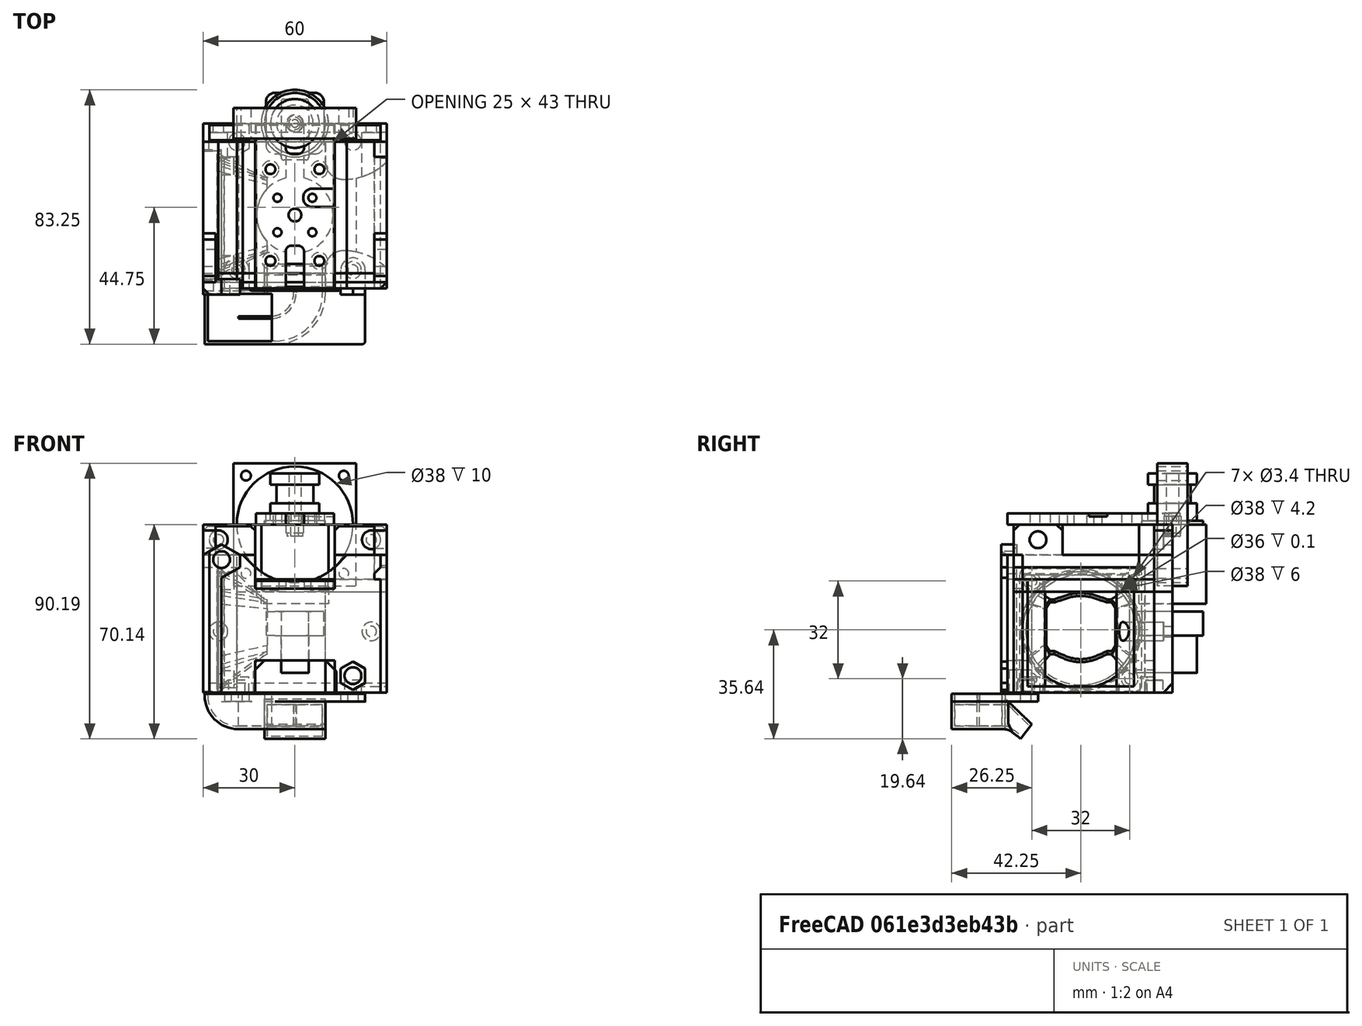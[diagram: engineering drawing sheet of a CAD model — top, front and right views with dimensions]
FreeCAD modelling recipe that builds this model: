
FCSTD DOCUMENT  (FreeCAD 1.0R39319 (Git))
Label: TAZ-EVO-Dragon-v0.4
License: All rights reserved
LicenseURL: https://en.wikipedia.org/wiki/All_rights_reserved
objects: Sketcher::SketchObject×53, PartDesign::Body×28, PartDesign::Pad×24, PartDesign::Pocket×20, App::Part×18, PartDesign::SubShapeBinder×17, PartDesign::FeatureBase×14, PartDesign::Fillet×11, PartDesign::Chamfer×9, PartDesign::Hole×5, PartDesign::Plane×4, App::DocumentObjectGroup×3, PartDesign::AdditiveLoft×2, PartDesign::Revolution×1, Mesh::Feature×1, PartDesign::Mirrored×1, PartDesign::Boolean×1, Spreadsheet::Sheet×1
note: 403 computed .brp shape members not serialized (recipe doc carries the construction recipe); baked Part::Feature solids carry a one-line shape summary decoded from their .brp

FEATURE [Sketcher::SketchObject] Sketch  label="Mount Plate Sk"
  ArcFitTolerance = 1e-06
  FullyConstrained = true
  MakeInternals = false
  Placement = pos=(0,0,0) rot=(1,0,0;1.5708rad)
  sketch-geometry (18):
    g0: LineSegment StartX=-30 StartY=55 StartZ=0 EndX=-30 EndY=-55 EndZ=0
    g1: LineSegment StartX=-30 StartY=-55 StartZ=0 EndX=30 EndY=-55 EndZ=0
    g2: LineSegment StartX=30 StartY=-55 StartZ=0 EndX=30 EndY=55 EndZ=0
    g3: LineSegment StartX=30 StartY=55 StartZ=0 EndX=-30 EndY=55 EndZ=0
    g4: Circle CenterX=-18 CenterY=50 CenterZ=0 NormalX=0 NormalY=0 NormalZ=1 AngleXU=0 Radius=1.7
    g5: Circle CenterX=18 CenterY=50 CenterZ=0 NormalX=0 NormalY=0 NormalZ=1 AngleXU=0 Radius=1.7
    g6: Circle CenterX=-18 CenterY=-50 CenterZ=0 NormalX=0 NormalY=0 NormalZ=1 AngleXU=0 Radius=1.7
    g7: Circle CenterX=18 CenterY=-50 CenterZ=0 NormalX=0 NormalY=0 NormalZ=1 AngleXU=0 Radius=1.7
    g8: Circle CenterX=-25 CenterY=35 CenterZ=0 NormalX=0 NormalY=0 NormalZ=1 AngleXU=0 Radius=1.7
    g9: Circle CenterX=-25 CenterY=5 CenterZ=0 NormalX=0 NormalY=0 NormalZ=1 AngleXU=0 Radius=1.7
    g10: Circle CenterX=-25 CenterY=-5 CenterZ=0 NormalX=0 NormalY=0 NormalZ=1 AngleXU=0 Radius=1.7
    g11: Circle CenterX=-25 CenterY=-35 CenterZ=0 NormalX=0 NormalY=0 NormalZ=1 AngleXU=0 Radius=1.7
    g12: Circle CenterX=25 CenterY=35 CenterZ=0 NormalX=0 NormalY=0 NormalZ=1 AngleXU=0 Radius=1.7
    g13: Circle CenterX=25 CenterY=5 CenterZ=0 NormalX=0 NormalY=0 NormalZ=1 AngleXU=0 Radius=1.7
    g14: Circle CenterX=25 CenterY=-5 CenterZ=0 NormalX=0 NormalY=0 NormalZ=1 AngleXU=0 Radius=1.7
    g15: Circle CenterX=25 CenterY=-35 CenterZ=0 NormalX=0 NormalY=0 NormalZ=1 AngleXU=0 Radius=1.7
    g16: LineSegment [constr] StartX=-25 StartY=35 StartZ=0 EndX=-25 EndY=-35 EndZ=0
    g17: LineSegment [constr] StartX=25 StartY=35 StartZ=0 EndX=25 EndY=-35 EndZ=0
  constraints (41):
    c: Coincident(g0,g1)
    c: Coincident(g1,g2)
    c: Coincident(g2,g3)
    c: Coincident(g3,g0)
    c: Vertical(g0)
    c: Horizontal(g3)
    c: DistanceX(g3,g3) = 60
    c: Symmetric(g8,g12,g-2)
    c: Symmetric(g11,g15,g-2)
    c: DistanceX(g8,g12) = 50
    c: Symmetric(g4,g5,g-2)
    c: DistanceX(g4,g5) = 36
    c: Symmetric(g11,g8,g-1)
    c: Coincident(g16,g8)
    c: Coincident(g16,g11)
    c: Coincident(g17,g12)
    c: Coincident(g17,g15)
    c: PointOnObject(g9,g16)
    c: DistanceY(g10,g9) = 10
    c: Symmetric(g6,g7,g-2)
    c: Symmetric(g6,g4,g-1)
    c: DistanceY(g6,g4) = 100
    c: Symmetric(g0,g1,g-2)
    c: Symmetric(g1,g2,g-1)
    c: DistanceY(g13,g12) = 30
    c: Equal(g8,g12)
    c: Equal(g9,g13)
    c: Equal(g10,g14)
    c: Equal(g11,g15)
    c: Equal(g6,g7)
    c: DistanceY(g2,g2) = 110
    c: Diameter(g13) = 3.4
    c: Equal(g5,g4)
    c: Equal(g13,g14)
    c: Equal(g14,g15)
    c: Equal(g15,g7)
    c: Equal(g5,g7)
    c: Equal(g13,g12)
    c: Symmetric(g9,g13,g-2)
    c: Symmetric(g13,g14,g-1)
    c: Symmetric(g9,g10,g-1)
FEATURE [Sketcher::SketchObject] Sketch001
  ArcFitTolerance = 1e-06
  AttachmentSupport = -> [XY_Plane001]
  FullyConstrained = true
  MakeInternals = false
  MapMode = 5
  sketch-geometry (1):
    g0: Circle CenterX=0 CenterY=0 CenterZ=0 NormalX=0 NormalY=0 NormalZ=1 AngleXU=0 Radius=11
  constraints (2):
    c: Coincident(g0,g-1)
    c: Diameter(g0) = 22
FEATURE [PartDesign::Pad] Pad
  Direction = (0,0,1)
  Length = 26
  Length2 = 10
  Profile = -> Sketch001
  ReferenceAxis = -> Sketch001 [N_Axis]
  Refine = true
  Reversed = true
  Suppressed = false
  Type = 0
FEATURE [PartDesign::Body] Body  label="HeatBreak"
  AllowCompound = false
  Group = -> [Sketch001,Pad]
  Origin = -> Origin001
  Tip = -> Pad
FEATURE [Sketcher::SketchObject] Sketch002
  ArcFitTolerance = 1e-06
  AttachmentSupport = -> [XZ_Plane002]
  FullyConstrained = true
  MakeInternals = false
  MapMode = 5
  Placement = pos=(0,0,0) rot=(1,0,0;1.5708rad)
  sketch-geometry (9):
    g0: LineSegment StartX=-9.5 StartY=0 StartZ=0 EndX=-9.5 EndY=-7.85 EndZ=0
    g1: LineSegment StartX=-9.5 StartY=-7.85 StartZ=0 EndX=-4.5 EndY=-7.85 EndZ=0
    g2: LineSegment StartX=-4.5 StartY=-7.85 StartZ=0 EndX=-4.5 EndY=-20 EndZ=0
    g3: LineSegment StartX=-4.5 StartY=-20 StartZ=0 EndX=4.5 EndY=-20 EndZ=0
    g4: LineSegment StartX=4.5 StartY=-20 StartZ=0 EndX=4.5 EndY=-7.85 EndZ=0
    g5: LineSegment StartX=4.5 StartY=-7.85 StartZ=0 EndX=9.5 EndY=-7.85 EndZ=0
    g6: LineSegment StartX=9.5 StartY=-7.85 StartZ=0 EndX=9.5 EndY=0 EndZ=0
    g7: LineSegment StartX=9.5 StartY=0 StartZ=0 EndX=-9.5 EndY=0 EndZ=0
    g8: LineSegment [constr] StartX=-4.5 StartY=-7.85 StartZ=0 EndX=4.5 EndY=-7.85 EndZ=0
  constraints (24):
    c: PointOnObject(g0,g-1)
    c: Vertical(g0)
    c: Coincident(g0,g1)
    c: Coincident(g1,g2)
    c: Vertical(g2)
    c: Coincident(g2,g3)
    c: Coincident(g3,g4)
    c: Vertical(g4)
    c: Coincident(g4,g5)
    c: Coincident(g5,g6)
    c: Vertical(g6)
    c: Coincident(g6,g7)
    c: Coincident(g7,g0)
    c: Coincident(g8,g1)
    c: Coincident(g8,g4)
    c: Horizontal(g8)
    c: Horizontal(g5)
    c: Horizontal(g1)
    c: Symmetric(g2,g3,g-2)
    c: Symmetric(g0,g6,g-2)
    c: DistanceY(g3,g6) = 20
    c: DistanceX(g3,g3) = 9
    c: DistanceX(g7,g7) = 19
    c: DistanceY(g0,g0) = 7.85
FEATURE [PartDesign::Pad] Pad001
  Direction = (0,-1,2e-16)
  Length = 20
  Length2 = 10
  Midplane = true
  Placement = pos=(0,0,0) rot=(1,0,0;1.5708rad)
  Profile = -> Sketch002
  ReferenceAxis = -> Sketch002 [N_Axis]
  Refine = true
  Suppressed = false
  Type = 0
FEATURE [Sketcher::SketchObject] Sketch003
  ArcFitTolerance = 1e-06
  AttachmentSupport = -> [Pad001]
  ExternalGeometry = -> [Pad001]
  FullyConstrained = true
  MakeInternals = false
  MapMode = 5
  Placement = pos=(0,-10,0) rot=(1,0,0;1.5708rad)
  sketch-geometry (4):
    g0: LineSegment StartX=-4.5 StartY=-20 StartZ=0 EndX=4.5 EndY=-20 EndZ=0
    g1: LineSegment StartX=4.5 StartY=-20 StartZ=0 EndX=4.5 EndY=0 EndZ=0
    g2: LineSegment StartX=4.5 StartY=0 StartZ=0 EndX=-4.5 EndY=0 EndZ=0
    g3: LineSegment StartX=-4.5 StartY=0 StartZ=0 EndX=-4.5 EndY=-20 EndZ=0
  constraints (10):
    c: Coincident(g0,g1)
    c: Coincident(g1,g2)
    c: Coincident(g2,g3)
    c: Coincident(g3,g0)
    c: Horizontal(g2)
    c: Vertical(g1)
    c: Vertical(g3)
    c: Coincident(g0,g-3)
    c: PointOnObject(g1,g-1)
    c: Coincident(g0,g-3)
FEATURE [PartDesign::Pad] Pad002
  BaseFeature = -> Pad001
  Direction = (0,-1,2e-16)
  Length = 2
  Length2 = 10
  Placement = pos=(0,0,0) rot=(1,0,0;1.5708rad)
  Profile = -> Sketch003
  ReferenceAxis = -> Sketch003 [N_Axis]
  Refine = true
  Suppressed = false
  Type = 0
FEATURE [Sketcher::SketchObject] Sketch004
  ArcFitTolerance = 1e-06
  AttachmentSupport = -> [Pad002]
  ExternalGeometry = -> [Pad002]
  FullyConstrained = true
  MakeInternals = false
  MapMode = 5
  Placement = pos=(0,10,0) rot=(-1,0,0;1.5708rad)
  sketch-geometry (4):
    g0: LineSegment StartX=-4.5 StartY=20 StartZ=0 EndX=-4.5 EndY=7.85 EndZ=0
    g1: LineSegment StartX=-4.5 StartY=7.85 StartZ=0 EndX=4.5 EndY=7.85 EndZ=0
    g2: LineSegment StartX=4.5 StartY=7.85 StartZ=0 EndX=4.5 EndY=20 EndZ=0
    g3: LineSegment StartX=4.5 StartY=20 StartZ=0 EndX=-4.5 EndY=20 EndZ=0
  constraints (10):
    c: Coincident(g0,g1)
    c: Coincident(g1,g2)
    c: Coincident(g2,g3)
    c: Coincident(g3,g0)
    c: Vertical(g0)
    c: Vertical(g2)
    c: Horizontal(g1)
    c: Horizontal(g3)
    c: Coincident(g0,g-3)
    c: Coincident(g1,g-4)
FEATURE [PartDesign::Pocket] Pocket
  BaseFeature = -> Pad002
  Direction = (0,-1,-2e-16)
  Length = 2
  Length2 = 5
  Placement = pos=(0,0,0) rot=(1,0,0;1.5708rad)
  Profile = -> Sketch004
  ReferenceAxis = -> Sketch004 [N_Axis]
  Refine = true
  Suppressed = false
  Type = 0
FEATURE [PartDesign::Fillet] Fillet
  Base = -> Pocket [Edge19,Edge23,Edge27,Edge21,Edge25,Edge15]
  BaseFeature = -> Pocket
  Placement = pos=(0,0,0) rot=(1,0,0;1.5708rad)
  Radius = 0.9
  Refine = true
  SupportTransform = false
  Suppressed = false
  UseAllEdges = false
FEATURE [PartDesign::Fillet] Fillet001
  Base = -> Fillet [Edge15,Edge19,Edge30,Edge26]
  BaseFeature = -> Fillet
  Placement = pos=(0,0,0) rot=(1,0,0;1.5708rad)
  Radius = 3
  Refine = true
  SupportTransform = false
  Suppressed = false
  UseAllEdges = false
FEATURE [PartDesign::Body] Body001  label="HeatBlock"
  AllowCompound = false
  Group = -> [Sketch002,Pad001,Sketch003,Pad002,Sketch004,Pocket,Fillet,Fillet001]
  Origin = -> Origin002
  Placement = pos=(0,0,-28.5) rot=(0,0,1;0rad)
  Tip = -> Fillet001
FEATURE [Sketcher::SketchObject] Sketch005
  ArcFitTolerance = 1e-06
  AttachmentSupport = -> [XZ_Plane003]
  FullyConstrained = true
  MakeInternals = false
  MapMode = 5
  Placement = pos=(0,0,0) rot=(1,0,0;1.5708rad)
  sketch-geometry (11):
    g0: LineSegment StartX=0 StartY=0 StartZ=0 EndX=10 EndY=0 EndZ=0
    g1: LineSegment StartX=10 StartY=0 StartZ=0 EndX=10 EndY=1.25 EndZ=0
    g2: LineSegment StartX=10 StartY=1.25 StartZ=0 EndX=8 EndY=1.25 EndZ=0
    g3: LineSegment StartX=8 StartY=1.25 StartZ=0 EndX=8 EndY=7 EndZ=0
    g4: LineSegment StartX=8 StartY=7 StartZ=0 EndX=6 EndY=7 EndZ=0
    g5: LineSegment StartX=6 StartY=7 StartZ=0 EndX=6 EndY=13.05 EndZ=0
    g6: LineSegment StartX=6 StartY=13.05 StartZ=0 EndX=8 EndY=13.05 EndZ=0
    g7: LineSegment StartX=8 StartY=13.05 StartZ=0 EndX=8 EndY=16.75 EndZ=0
    g8: LineSegment StartX=8 StartY=16.75 StartZ=0 EndX=0 EndY=16.75 EndZ=0
    g9: LineSegment StartX=0 StartY=16.75 StartZ=0 EndX=0 EndY=0 EndZ=0
    g10: LineSegment [constr] StartX=8 StartY=13.05 StartZ=0 EndX=8 EndY=7 EndZ=0
  constraints (31):
    c: Coincident(g-1,g0)
    c: PointOnObject(g0,g-1)
    c: Coincident(g0,g1)
    c: Vertical(g1)
    c: Coincident(g1,g2)
    c: Horizontal(g2)
    c: Coincident(g2,g3)
    c: Coincident(g3,g4)
    c: Horizontal(g4)
    c: Coincident(g4,g5)
    c: Vertical(g5)
    c: Coincident(g5,g6)
    c: Horizontal(g6)
    c: Coincident(g6,g7)
    c: Coincident(g7,g8)
    c: Horizontal(g8)
    c: Coincident(g8,g9)
    c: Coincident(g9,g0)
    c: Vertical(g9)
    c: DistanceX(g0,g0) = 10
    c: DistanceY(g1,g1) = 1.25
    c: Vertical(g3)
    c: DistanceY(g0,g3) = 7
    c: Vertical(g7)
    c: DistanceY(g9,g9) = 16.75
    c: DistanceY(g7,g7) = 3.7
    c: DistanceX(g8,g8) = 8
    c: Coincident(g10,g6)
    c: Coincident(g10,g3)
    c: Vertical(g10)
    c: DistanceX(g0,g4) = 6
FEATURE [PartDesign::Revolution] Revolution
  Angle = 360
  Angle2 = 60
  Axis = (0,2e-16,1)
  Base = (0,0,0)
  Placement = pos=(0,0,0) rot=(1,0,0;1.5708rad)
  Profile = -> Sketch005
  ReferenceAxis = -> Sketch005 [V_Axis]
  Refine = true
  Reversed = true
  Suppressed = false
  Type = 0
FEATURE [PartDesign::Hole] Hole
  BaseFeature = -> Revolution
  CustomThreadClearance = 0
  Depth = 25
  DepthType = 0
  Diameter = 4
  DrillForDepth = false
  DrillPoint = 1
  DrillPointAngle = 118
  HoleCutCountersinkAngle = 90
  HoleCutCustomValues = false
  HoleCutDepth = 0
  HoleCutDiameter = 6.1
  HoleCutType = 0
  ModelThread = false
  Placement = pos=(0,0,0) rot=(1,0,0;1.5708rad)
  Profile = -> Revolution [Face9]
  Refine = true
  Suppressed = false
  Tapered = false
  TaperedAngle = 90
  ThreadClass = 0
  ThreadDepth = 25
  ThreadDepthType = 0
  ThreadDirection = 0
  ThreadFit = 0
  ThreadSize = 0
  ThreadType = 0
  Threaded = false
  UseCustomThreadClearance = false
FEATURE [PartDesign::Body] Body002  label="Adapter"
  AllowCompound = false
  Group = -> [Sketch005,Revolution,Hole]
  Origin = -> Origin003
  Tip = -> Hole
FEATURE [App::Part] Part  label="Hotend"
  Group = -> [Body,Body001,Body002]
  Origin = -> Origin
  Placement = pos=(0,-30,-18.5) rot=(0,0,1;0rad)
FEATURE [Sketcher::SketchObject] Sketch006  label="FilamentPath"
  ArcFitTolerance = 1e-06
  FullyConstrained = true
  MakeInternals = false
  sketch-geometry (1):
    g0: Circle CenterX=0 CenterY=-30 CenterZ=0 NormalX=0 NormalY=0 NormalZ=1 AngleXU=0 Radius=0.875
  constraints (3):
    c: PointOnObject(g0,g-2)
    c: Diameter(g0) = 1.75
    c: DistanceY(g0,g-1) = 30
FEATURE [Sketcher::SketchObject] Sketch008
  ArcFitTolerance = 1e-06
  AttachmentSupport = -> [XZ_Plane007]
  FullyConstrained = true
  MakeInternals = false
  MapMode = 5
  Placement = pos=(0,0,0) rot=(1,0,0;1.5708rad)
  sketch-geometry (13):
    g0: Circle CenterX=0 CenterY=0 CenterZ=0 NormalX=0 NormalY=0 NormalZ=1 AngleXU=0 Radius=19
    g1: LineSegment StartX=-20.05 StartY=20.05 StartZ=0 EndX=-20.05 EndY=-20.05 EndZ=0
    g2: LineSegment StartX=-20.05 StartY=-20.05 StartZ=0 EndX=20.05 EndY=-20.05 EndZ=0
    g3: LineSegment StartX=20.05 StartY=-20.05 StartZ=0 EndX=20.05 EndY=20.05 EndZ=0
    g4: LineSegment StartX=20.05 StartY=20.05 StartZ=0 EndX=-20.05 EndY=20.05 EndZ=0
    g5: Circle CenterX=-16 CenterY=16 CenterZ=0 NormalX=0 NormalY=0 NormalZ=1 AngleXU=0 Radius=1.6
    g6: Circle CenterX=-16 CenterY=-16 CenterZ=0 NormalX=0 NormalY=0 NormalZ=1 AngleXU=0 Radius=1.6
    g7: Circle CenterX=16 CenterY=-16 CenterZ=0 NormalX=0 NormalY=0 NormalZ=1 AngleXU=0 Radius=1.6
    g8: Circle CenterX=16 CenterY=16 CenterZ=0 NormalX=0 NormalY=0 NormalZ=1 AngleXU=0 Radius=1.6
    g9: LineSegment [constr] StartX=-16 StartY=16 StartZ=0 EndX=16 EndY=16 EndZ=0
    g10: LineSegment [constr] StartX=16 StartY=16 StartZ=0 EndX=16 EndY=-16 EndZ=0
    g11: LineSegment [constr] StartX=16 StartY=-16 StartZ=0 EndX=-16 EndY=-16 EndZ=0
    g12: LineSegment [constr] StartX=-16 StartY=-16 StartZ=0 EndX=-16 EndY=16 EndZ=0
  constraints (30):
    c: Coincident(g0,g-1)
    c: Coincident(g1,g2)
    c: Coincident(g2,g3)
    c: Coincident(g3,g4)
    c: Coincident(g4,g1)
    c: Vertical(g1)
    c: Horizontal(g2)
    c: DistanceY(g3,g3) = 40.1
    c: Equal(g3,g2)
    c: Symmetric(g3,g2,g-1)
    c: Symmetric(g3,g1,g-2)
    c: Diameter(g0) = 38
    c: Coincident(g9,g5)
    c: Coincident(g9,g8)
    c: Horizontal(g9)
    c: Coincident(g10,g8)
    c: Coincident(g10,g7)
    c: Vertical(g10)
    c: Coincident(g11,g7)
    c: Coincident(g11,g6)
    c: Coincident(g12,g6)
    c: Coincident(g12,g5)
    c: DistanceY(g12,g12) = 32
    c: Equal(g12,g9)
    c: Symmetric(g7,g6,g-2)
    c: Symmetric(g6,g5,g-1)
    c: Equal(g6,g5)
    c: Equal(g5,g8)
    c: Equal(g5,g7)
    c: Diameter(g6) = 3.2
FEATURE [PartDesign::Pad] Pad003
  Direction = (0,-1,2e-16)
  Length = 10
  Length2 = 10
  Midplane = true
  Placement = pos=(0,0,0) rot=(1,0,0;1.5708rad)
  Profile = -> Sketch008
  ReferenceAxis = -> Sketch008 [N_Axis]
  Refine = true
  Suppressed = false
  Type = 0
FEATURE [PartDesign::Body] Body004
  AllowCompound = false
  Group = -> [Sketch008,Pad003]
  Origin = -> Origin007
  Placement = pos=(0,-1.8e-15,6e-16) rot=(0,0,1;0rad)
  Tip = -> Pad003
FEATURE [App::Part] Part003  label="4010 Cooling"
  Group = -> [Body004]
  Origin = -> Origin008
  Placement = pos=(-30,-30,-34.5) rot=(0,0,1;4.71239rad)
FEATURE [Mesh::Feature] Radial_Fan_50x15_v8
  Placement = pos=(-44,6,92) rot=(0,0,1;0rad)
FEATURE [App::Part] Part004  label="5015 Part"
  Group = -> [Radial_Fan_50x15_v8]
  Origin = -> Origin010
  Placement = pos=(-28.5,-71,-57) rot=(1,0,0;1.5708rad)
FEATURE [App::DocumentObjectGroup] Group001  label="Fans"
  Group = -> [Part003,Part004]
FEATURE [Sketcher::SketchObject] Sketch011
  ArcFitTolerance = 1e-06
  AttachmentSupport = -> [XY_Plane012]
  FullyConstrained = true
  MakeInternals = false
  MapMode = 5
  sketch-geometry (1):
    g0: Circle CenterX=0 CenterY=0 CenterZ=0 NormalX=0 NormalY=0 NormalZ=1 AngleXU=0 Radius=2.8
  constraints (2):
    c: Diameter(g0) = 5.6
    c: Coincident(g0,g-1)
FEATURE [PartDesign::Pad] Pad005
  Direction = (0,0,1)
  Length = 3.8
  Length2 = 10
  Profile = -> Sketch011
  ReferenceAxis = -> Sketch011 [N_Axis]
  Refine = true
  Suppressed = false
  Type = 0
FEATURE [PartDesign::Hole] Hole001
  BaseFeature = -> Pad005
  CustomThreadClearance = 0
  Depth = 17.7438
  DepthType = 0
  Diameter = 2.5
  DrillForDepth = false
  DrillPoint = 1
  DrillPointAngle = 118
  HoleCutCountersinkAngle = 90
  HoleCutCustomValues = false
  HoleCutDepth = 0
  HoleCutDiameter = 6.1
  HoleCutType = 0
  ModelThread = false
  Profile = -> Pad005 [Edge3]
  Refine = true
  Suppressed = false
  Tapered = false
  TaperedAngle = 90
  ThreadClass = 0
  ThreadDepth = 17.7438
  ThreadDepthType = 0
  ThreadDirection = 0
  ThreadFit = 1
  ThreadSize = 9
  ThreadType = 1
  Threaded = true
  UseCustomThreadClearance = false
FEATURE [Sketcher::SketchObject] Sketch012
  ArcFitTolerance = 1e-06
  AttachmentSupport = -> [Hole001]
  ExternalGeometry = -> [Hole001]
  FullyConstrained = false
  MakeInternals = false
  MapMode = 5
  Placement = pos=(0,0,3.8) rot=(0,0,1;0rad)
  sketch-geometry (2):
    g0: Circle CenterX=0 CenterY=0 CenterZ=0 NormalX=0 NormalY=0 NormalZ=1 AngleXU=0 Radius=2.575
    g1: Circle CenterX=0 CenterY=0 CenterZ=0 NormalX=0 NormalY=0 NormalZ=1 AngleXU=0 Radius=2.8
  constraints (3):
    c: Coincident(g0,g-1)
    c: Diameter(g0) = 5.15
    c: Coincident(g1,g0)
FEATURE [PartDesign::Pocket] Pocket001
  BaseFeature = -> Hole001
  Direction = (0,0,-1)
  Length = 1
  Length2 = 5
  Profile = -> Sketch012
  ReferenceAxis = -> Sketch012 [N_Axis]
  Refine = true
  Suppressed = false
  Type = 0
FEATURE [PartDesign::Body] Body006  label="M3InsertBody01"
  AllowCompound = false
  Group = -> [Sketch011,Pad005,Hole001,Sketch012,Pocket001]
  Origin = -> Origin012
  Tip = -> Pocket001
FEATURE [App::Part] Part005  label="Insert001"
  Group = -> [Body006]
  Origin = -> Origin011
  Placement = pos=(-18,-52,-12) rot=(1,0,0;4.71239rad)
FEATURE [PartDesign::FeatureBase] Clone001
  BaseFeature = -> Body006
  Suppressed = false
FEATURE [PartDesign::Body] Body007
  AllowCompound = false
  Group = -> [Clone001]
  Origin = -> Origin014
  Tip = -> Clone001
FEATURE [App::Part] Part006  label="Insert002"
  Group = -> [Body007]
  Origin = -> Origin013
  Placement = pos=(25,-52,-50) rot=(0.57735,-0.57735,-0.57735;4.18879rad)
FEATURE [PartDesign::FeatureBase] Clone002
  BaseFeature = -> Body006
  Suppressed = false
FEATURE [PartDesign::Body] Body008
  AllowCompound = false
  Group = -> [Clone002]
  Origin = -> Origin016
  Tip = -> Clone002
FEATURE [App::Part] Part007  label="Insert003"
  Group = -> [Body008]
  Origin = -> Origin015
  Placement = pos=(-25,-42,-18.5) rot=(-0.707107,0,-0.707107;3.14159rad)
FEATURE [PartDesign::FeatureBase] Clone003
  BaseFeature = -> Body006
  Suppressed = false
FEATURE [PartDesign::Body] Body009
  AllowCompound = false
  Group = -> [Clone003]
  Origin = -> Origin018
  Tip = -> Clone003
FEATURE [App::Part] Part008  label="Insert004"
  Group = -> [Body009]
  Origin = -> Origin017
  Placement = pos=(-25,-10,-18.5) rot=(-0.707107,0,-0.707107;3.14159rad)
FEATURE [PartDesign::FeatureBase] Clone004
  BaseFeature = -> Body007
  Suppressed = false
FEATURE [PartDesign::Body] Body011
  AllowCompound = false
  Group = -> [Clone004]
  Origin = -> Origin022
  Tip = -> Clone004
FEATURE [App::Part] Part010  label="Insert005"
  Group = -> [Body011]
  Origin = -> Origin021
  Placement = pos=(-14.5,-41,-18) rot=(0,1,0;3.14159rad)
FEATURE [PartDesign::FeatureBase] Clone005
  BaseFeature = -> Body007
  Suppressed = false
FEATURE [PartDesign::Body] Body012
  AllowCompound = false
  Group = -> [Clone005]
  Origin = -> Origin024
  Tip = -> Clone005
FEATURE [App::Part] Part011  label="Insert006"
  Group = -> [Body012]
  Origin = -> Origin023
  Placement = pos=(-14.5,-19,-18) rot=(0,1,0;3.14159rad)
FEATURE [PartDesign::FeatureBase] Clone006
  BaseFeature = -> Body007
  Suppressed = false
FEATURE [PartDesign::Body] Body013
  AllowCompound = false
  Group = -> [Clone006]
  Origin = -> Origin027
  Placement = pos=(0,0,0) rot=(1,0,0;3.14159rad)
  Tip = -> Clone006
FEATURE [App::Part] Part012
  Group = -> [Body013]
  Origin = -> Origin025
  Placement = pos=(14.5,-19,-18) rot=(0,0,1;0rad)
FEATURE [PartDesign::FeatureBase] Clone007
  BaseFeature = -> Body007
  Suppressed = false
FEATURE [PartDesign::Body] Body014
  AllowCompound = false
  Group = -> [Clone007]
  Origin = -> Origin028
  Placement = pos=(0,0,0) rot=(1,0,0;3.14159rad)
  Tip = -> Clone007
FEATURE [App::Part] Part013
  Group = -> [Body014]
  Origin = -> Origin026
  Placement = pos=(14.5,-41,-18) rot=(0,0,1;0rad)
FEATURE [Sketcher::SketchObject] Sketch031
  ArcFitTolerance = 1e-06
  AttachmentSupport = -> [XY_Plane030]
  FullyConstrained = true
  MakeInternals = false
  MapMode = 5
  sketch-geometry (7):
    g0: LineSegment StartX=-12.75 StartY=0 StartZ=0 EndX=-12.75 EndY=-5 EndZ=0
    g1: LineSegment StartX=-12.75 StartY=-54 StartZ=0 EndX=12.75 EndY=-54 EndZ=0
    g2: LineSegment StartX=12.75 StartY=-5 StartZ=0 EndX=12.75 EndY=0 EndZ=0
    g3: LineSegment StartX=12.75 StartY=0 StartZ=0 EndX=-12.75 EndY=0 EndZ=0
    g4: LineSegment StartX=-12.75 StartY=-5 StartZ=0 EndX=-12.75 EndY=-54 EndZ=0
    g5: LineSegment [constr] StartX=-12.75 StartY=-5 StartZ=0 EndX=12.75 EndY=-5 EndZ=0
    g6: LineSegment StartX=12.75 StartY=-5 StartZ=0 EndX=12.75 EndY=-54 EndZ=0
  constraints (19):
    c: PointOnObject(g0,g-1)
    c: Vertical(g0)
    c: Horizontal(g1)
    c: Vertical(g2)
    c: Coincident(g2,g3)
    c: Coincident(g3,g0)
    c: Symmetric(g0,g2,g-2)
    c: DistanceY(g1,g2) = 54
    c: Coincident(g4,g0)
    c: Vertical(g4)
    c: Coincident(g5,g0)
    c: Vertical(g6)
    c: DistanceX(g5,g5) = 25.5
    c: Coincident(g6,g2)
    c: Coincident(g2,g5)
    c: Coincident(g4,g1)
    c: Coincident(g6,g1)
    c: Horizontal(g5)
    c: DistanceY(g0,g0) = 5
FEATURE [PartDesign::Pad] Pad008  label="BasePlate"
  Direction = (0,0,1)
  Length = 3.6
  Length2 = 10
  Profile = -> Sketch031
  ReferenceAxis = -> Sketch031 [N_Axis]
  Refine = true
  Suppressed = false
  Type = 0
FEATURE [PartDesign::SubShapeBinder] Binder  label="FilamentPathBinder"
  BindCopyOnChange = 0
  BindMode = 0
  ClaimChildren = false
  Context = -> Part014 [Body015.Binder.]
  Fuse = false
  MakeFace = true
  OffsetFill = false
  OffsetIntersection = false
  OffsetJoinType = 0
  OffsetOpenResult = false
  PartialLoad = false
  Refine = true
  Relative = true
  Support = -> [Sketch006]
  _Version = 2
FEATURE [Sketcher::SketchObject] Sketch032  label="DragonHotendScrewsSk"
  ArcFitTolerance = 1e-06
  AttachmentSupport = -> [Pad008]
  ExternalGeometry = -> [Binder]
  FullyConstrained = true
  MakeInternals = false
  MapMode = 5
  Placement = pos=(0,0,3.6) rot=(0,0,1;0rad)
  sketch-geometry (9):
    g0: Circle [constr] CenterX=0 CenterY=-30 CenterZ=0 NormalX=0 NormalY=0 NormalZ=1 AngleXU=0 Radius=8.02574
    g1: Circle CenterX=-5.7 CenterY=-24.35 CenterZ=0 NormalX=0 NormalY=0 NormalZ=1 AngleXU=0 Radius=1.325
    g2: Circle CenterX=5.7 CenterY=-24.35 CenterZ=0 NormalX=0 NormalY=0 NormalZ=1 AngleXU=0 Radius=1.325
    g3: Circle CenterX=5.7 CenterY=-35.65 CenterZ=0 NormalX=0 NormalY=0 NormalZ=1 AngleXU=0 Radius=1.325
    g4: Circle CenterX=-5.7 CenterY=-35.65 CenterZ=0 NormalX=0 NormalY=0 NormalZ=1 AngleXU=0 Radius=1.325
    g5: LineSegment [constr] StartX=-5.7 StartY=-24.35 StartZ=0 EndX=5.7 EndY=-24.35 EndZ=0
    g6: LineSegment [constr] StartX=-5.7 StartY=-24.35 StartZ=0 EndX=-5.7 EndY=-35.65 EndZ=0
    g7: LineSegment [constr] StartX=-5.7 StartY=-35.65 StartZ=0 EndX=5.7 EndY=-35.65 EndZ=0
    g8: LineSegment [constr] StartX=5.7 StartY=-35.65 StartZ=0 EndX=5.7 EndY=-24.35 EndZ=0
  constraints (22):
    c: Coincident(g0,g-3)
    c: PointOnObject(g1,g0)
    c: PointOnObject(g2,g0)
    c: PointOnObject(g3,g0)
    c: PointOnObject(g4,g0)
    c: Coincident(g5,g1)
    c: Coincident(g5,g2)
    c: Coincident(g6,g1)
    c: Coincident(g6,g4)
    c: Vertical(g6)
    c: Coincident(g7,g4)
    c: Coincident(g7,g3)
    c: Horizontal(g7)
    c: Coincident(g8,g3)
    c: Coincident(g8,g2)
    c: Horizontal(g5)
    c: DistanceX(g5,g5) = 11.4
    c: DistanceY(g8,g8) = 11.3
    c: Equal(g1,g2)
    c: Equal(g4,g3)
    c: Equal(g4,g1)
    c: Diameter(g1) = 2.65
FEATURE [Sketcher::SketchObject] Sketch034  label="WireCutoutSk"
  ArcFitTolerance = 1e-06
  AttachmentSupport = -> [Pad008]
  ExternalGeometry = -> [Pad008,Binder]
  FullyConstrained = true
  MakeInternals = false
  MapMode = 5
  Placement = pos=(0,0,3.6) rot=(0,0,1;0rad)
  sketch-geometry (10):
    g0: LineSegment StartX=-3 StartY=-54 StartZ=0 EndX=3 EndY=-54 EndZ=0
    g1: LineSegment StartX=3 StartY=-54 StartZ=0 EndX=3 EndY=-40 EndZ=0
    g2: LineSegment StartX=3 StartY=-40 StartZ=0 EndX=-3 EndY=-40 EndZ=0
    g3: LineSegment StartX=-3 StartY=-40 StartZ=0 EndX=-3 EndY=-54 EndZ=0
    g4: LineSegment StartX=-3 StartY=0 StartZ=0 EndX=-3 EndY=-10 EndZ=0
    g5: LineSegment StartX=-3 StartY=-10 StartZ=0 EndX=3 EndY=-10 EndZ=0
    g6: LineSegment StartX=3 StartY=-10 StartZ=0 EndX=3 EndY=0 EndZ=0
    g7: LineSegment StartX=3 StartY=0 StartZ=0 EndX=-3 EndY=0 EndZ=0
    g8: LineSegment [constr] StartX=-3 StartY=-10 StartZ=0 EndX=-3 EndY=-40 EndZ=0
    g9: LineSegment [constr] StartX=3 StartY=-10 StartZ=0 EndX=3 EndY=-40 EndZ=0
  constraints (26):
    c: Coincident(g0,g1)
    c: Coincident(g1,g2)
    c: Coincident(g2,g3)
    c: Coincident(g3,g0)
    c: Horizontal(g0)
    c: Vertical(g1)
    c: Vertical(g3)
    c: PointOnObject(g0,g-3)
    c: Coincident(g4,g5)
    c: Coincident(g5,g6)
    c: Coincident(g6,g7)
    c: Coincident(g7,g4)
    c: Vertical(g4)
    c: Vertical(g6)
    c: Horizontal(g7)
    c: PointOnObject(g4,g-4)
    c: DistanceX(g2,g2) = 6
    c: Symmetric(g2,g1,g-2)
    c: Symmetric(g4,g5,g-2)
    c: Coincident(g8,g4)
    c: Coincident(g8,g2)
    c: Coincident(g9,g5)
    c: Coincident(g9,g1)
    c: DistanceY(g5,g6) = 10
    c: DistanceY(g1,g1) = 14
    c: Vertical(g9)
FEATURE [Sketcher::SketchObject] Sketch035  label="FilamentPathSk"
  ArcFitTolerance = 1e-06
  AttachmentSupport = -> [Pad008]
  ExternalGeometry = -> [Binder]
  FullyConstrained = true
  MakeInternals = false
  MapMode = 5
  Placement = pos=(0,0,3.6) rot=(0,0,1;0rad)
  sketch-geometry (1):
    g0: Circle CenterX=0 CenterY=-30 CenterZ=0 NormalX=0 NormalY=0 NormalZ=1 AngleXU=0 Radius=2.1
  constraints (2):
    c: Diameter(g0) = 4.2
    c: Coincident(g0,g-3)
FEATURE [PartDesign::Pocket] Pocket014  label="WirePathCutout"
  BaseFeature = -> Pad008
  Direction = (0,0,-1)
  Length = 5
  Length2 = 5
  Profile = -> Sketch034
  ReferenceAxis = -> Sketch034 [N_Axis]
  Refine = true
  Suppressed = false
  Type = 0
FEATURE [PartDesign::Fillet] Fillet007
  Base = -> Pocket014 [Edge36,Edge17,Edge30,Edge31]
  BaseFeature = -> Pocket014
  Radius = 2
  Refine = true
  SupportTransform = false
  Suppressed = false
  UseAllEdges = false
FEATURE [PartDesign::FeatureBase] Clone
  BaseFeature = -> Body007
  Suppressed = false
FEATURE [PartDesign::Body] Body016
  AllowCompound = false
  Group = -> [Clone]
  Origin = -> Origin033
  Tip = -> Clone
FEATURE [App::Part] Part015
  Group = -> [Body016]
  Origin = -> Origin031
  Placement = pos=(16,-9,-55) rot=(0,0,1;0rad)
FEATURE [PartDesign::FeatureBase] Clone008
  BaseFeature = -> Body007
  Suppressed = false
FEATURE [PartDesign::Body] Body017
  AllowCompound = false
  Group = -> [Clone008]
  Origin = -> Origin034
  Tip = -> Clone008
FEATURE [App::Part] Part016
  Group = -> [Body017]
  Origin = -> Origin032
  Placement = pos=(-16,-9,-55) rot=(0,0,1;0rad)
FEATURE [App::DocumentObjectGroup] Group  label="Inserts"
  Group = -> [Part006,Part007,Part008,Part005,Part010,Part011,Part012,Part013,Part015,Part016]
FEATURE [PartDesign::Pocket] Pocket019  label="FilamentPathHole"
  BaseFeature = -> Fillet007
  Direction = (0,0,-1)
  Length = 5
  Length2 = 5
  Profile = -> Sketch035
  ReferenceAxis = -> Sketch035 [N_Axis]
  Refine = true
  Suppressed = false
  Type = 0
FEATURE [PartDesign::Pocket] Pocket020  label="DragonHotendScrewHoles"
  BaseFeature = -> Pocket019
  Direction = (0,0,-1)
  Length = 5
  Length2 = 5
  Profile = -> Sketch032
  ReferenceAxis = -> Sketch032 [N_Axis]
  Refine = true
  Suppressed = false
  Type = 0
FEATURE [Sketcher::SketchObject] Sketch042  label="CoolingDuct Base Sk"
  ArcFitTolerance = 1e-06
  FullyConstrained = true
  MakeInternals = false
  Placement = pos=(0,0,-55) rot=(0,0,1;0rad)
  expr: Constraints[2] = <<Properties>>.M3Inset
  sketch-geometry (8):
    g0: Circle CenterX=-19 CenterY=-6 CenterZ=0 NormalX=0 NormalY=0 NormalZ=1 AngleXU=0 Radius=2.75
    g1: Circle CenterX=19 CenterY=-6 CenterZ=0 NormalX=0 NormalY=0 NormalZ=1 AngleXU=0 Radius=2.75
    g2: Circle CenterX=-19 CenterY=-48 CenterZ=0 NormalX=0 NormalY=0 NormalZ=1 AngleXU=0 Radius=2.75
    g3: Circle CenterX=19 CenterY=-48 CenterZ=0 NormalX=0 NormalY=0 NormalZ=1 AngleXU=0 Radius=2.75
    g4: LineSegment [constr] StartX=-19 StartY=-6 StartZ=0 EndX=19 EndY=-6 EndZ=0
    g5: LineSegment [constr] StartX=-19 StartY=-48 StartZ=0 EndX=19 EndY=-48 EndZ=0
    g6: LineSegment [constr] StartX=19 StartY=-6 StartZ=0 EndX=19 EndY=-48 EndZ=0
    g7: LineSegment [constr] StartX=-19 StartY=-6 StartZ=0 EndX=-19 EndY=-48 EndZ=0
  constraints (20):
    c: Coincident(g4,g0)
    c: Coincident(g4,g1)
    c: Diameter(g0) = 5.5
    c: Equal(g0,g1)
    c: DistanceY(g1,g-1) = 6
    c: Equal(g2,g0)
    c: Equal(g3,g2)
    c: Coincident(g5,g2)
    c: Coincident(g5,g3)
    c: Horizontal(g5)
    c: DistanceY(g3,g1) = 42
    c: DistanceX(g2,g3) = 38
    c: Coincident(g6,g1)
    c: Coincident(g6,g3)
    c: Vertical(g6)
    c: Horizontal(g4)
    c: Coincident(g7,g0)
    c: Coincident(g7,g2)
    c: Vertical(g7)
    c: DistanceX(g0,g-1) = 19
FEATURE [Sketcher::SketchObject] Sketch043  label="Tool Bottom Base Sk"
  ArcFitTolerance = 1e-06
  FullyConstrained = true
  MakeInternals = false
  Placement = pos=(0,0,-55) rot=(0,0,1;0rad)
  sketch-geometry (4):
    g0: LineSegment StartX=-30 StartY=-52 StartZ=0 EndX=30 EndY=-52 EndZ=0
    g1: LineSegment StartX=30 StartY=-52 StartZ=0 EndX=30 EndY=0 EndZ=0
    g2: LineSegment StartX=30 StartY=0 StartZ=0 EndX=-30 EndY=0 EndZ=0
    g3: LineSegment StartX=-30 StartY=0 StartZ=0 EndX=-30 EndY=-52 EndZ=0
  constraints (11):
    c: Coincident(g0,g1)
    c: Coincident(g1,g2)
    c: Coincident(g2,g3)
    c: Coincident(g3,g0)
    c: Horizontal(g0)
    c: Vertical(g1)
    c: Vertical(g3)
    c: PointOnObject(g1,g-1)
    c: DistanceX(g0,g0) = 60
    c: DistanceY(g1,g1) = 52
    c: Symmetric(g2,g1,g-2)
FEATURE [Sketcher::SketchObject] Sketch045  label="Mount Plate Base Sk"
  ArcFitTolerance = 1e-06
  FullyConstrained = true
  MakeInternals = false
  Placement = pos=(0,0,-18) rot=(0,0,1;0rad)
  expr: Constraints[13] = <<Properties>>.M3Inset
  sketch-geometry (9):
    g0: Circle CenterX=-8 CenterY=-15 CenterZ=0 NormalX=0 NormalY=0 NormalZ=1 AngleXU=0 Radius=2.75
    g1: Circle CenterX=8 CenterY=-15 CenterZ=0 NormalX=0 NormalY=0 NormalZ=1 AngleXU=0 Radius=2.75
    g2: Circle CenterX=8 CenterY=-45 CenterZ=0 NormalX=0 NormalY=0 NormalZ=1 AngleXU=0 Radius=2.75
    g3: Circle CenterX=-8 CenterY=-45 CenterZ=0 NormalX=0 NormalY=0 NormalZ=1 AngleXU=0 Radius=2.75
    g4: LineSegment [constr] StartX=-8 StartY=-15 StartZ=0 EndX=8 EndY=-15 EndZ=0
    g5: LineSegment [constr] StartX=8 StartY=-15 StartZ=0 EndX=8 EndY=-45 EndZ=0
    g6: LineSegment [constr] StartX=8 StartY=-45 StartZ=0 EndX=-8 EndY=-45 EndZ=0
    g7: LineSegment [constr] StartX=-8 StartY=-45 StartZ=0 EndX=-8 EndY=-15 EndZ=0
    g8: LineSegment [constr] StartX=-8 StartY=-30 StartZ=0 EndX=8 EndY=-30 EndZ=0
  constraints (21):
    c: Coincident(g4,g0)
    c: Coincident(g4,g1)
    c: Coincident(g5,g1)
    c: Coincident(g5,g2)
    c: Vertical(g5)
    c: Coincident(g6,g2)
    c: Coincident(g6,g3)
    c: Horizontal(g6)
    c: Coincident(g7,g3)
    c: Coincident(g7,g0)
    c: Vertical(g7)
    c: Symmetric(g0,g1,g-2)
    c: Equal(g0,g3)
    c: Diameter(g3) = 5.5
    c: Equal(g3,g2)
    c: Equal(g2,g1)
    c: Symmetric(g7,g7,g8)
    c: Symmetric(g5,g5,g8)
    c: DistanceY(g5,g5) = 30
    c: DistanceX(g4,g4) = 16
    c: DistanceY(g8,g-1) = 30
FEATURE [Sketcher::SketchObject] Sketch046  label="Part Fan Base Sk"
  ArcFitTolerance = 1e-06
  FullyConstrained = true
  MakeInternals = false
  Placement = pos=(0,-52,0) rot=(1,0,0;1.5708rad)
  expr: Constraints[9] = <<Properties>>.M3Inset
  sketch-geometry (4):
    g0: Circle CenterX=19 CenterY=-49.5 CenterZ=0 NormalX=0 NormalY=0 NormalZ=1 AngleXU=0 Radius=2.75
    g1: Circle CenterX=-24 CenterY=-11.5 CenterZ=0 NormalX=0 NormalY=0 NormalZ=1 AngleXU=0 Radius=2.75
    g2: LineSegment [constr] StartX=-24 StartY=-11.5 StartZ=0 EndX=19 EndY=-11.5 EndZ=0
    g3: LineSegment [constr] StartX=19 StartY=-11.5 StartZ=0 EndX=19 EndY=-49.5 EndZ=0
  constraints (11):
    c: Coincident(g2,g1)
    c: Horizontal(g2)
    c: Coincident(g3,g2)
    c: Coincident(g3,g0)
    c: Vertical(g3)
    c: DistanceY(g3,g3) = 38
    c: DistanceX(g2,g2) = 43
    c: DistanceX(g1,g-1) = 24
    c: Equal(g1,g0)
    c: Diameter(g0) = 5.5
    c: DistanceY(g2,g-1) = 11.5
FEATURE [PartDesign::SubShapeBinder] Binder003  label="ToolBottomBinder001"
  BindCopyOnChange = 0
  BindMode = 0
  ClaimChildren = false
  Context = -> Part017 [Body018.Binder003.]
  Fuse = false
  MakeFace = true
  OffsetFill = false
  OffsetIntersection = false
  OffsetJoinType = 0
  OffsetOpenResult = false
  PartialLoad = false
  Refine = true
  Relative = true
  Support = -> [Sketch043]
  _Version = 2
FEATURE [Sketcher::SketchObject] Sketch047  label="Exhaust Pd"
  ArcFitTolerance = 1e-06
  AttachmentSupport = -> [Binder003]
  ExternalGeometry = -> [Binder003]
  FullyConstrained = true
  MakeInternals = false
  MapMode = 5
  Placement = pos=(0,0,-55) rot=(0,0,1;0rad)
  sketch-geometry (8):
    g0: LineSegment StartX=10 StartY=-46 StartZ=0 EndX=10 EndY=-52 EndZ=0
    g1: LineSegment StartX=10 StartY=-52 StartZ=0 EndX=30 EndY=-52 EndZ=0
    g2: LineSegment StartX=30 StartY=-52 StartZ=0 EndX=30 EndY=-47.3926 EndZ=0
    g3: ArcOfCircle CenterX=16 CenterY=-48 CenterZ=0 NormalX=0 NormalY=0 NormalZ=1 AngleXU=0 Radius=6.32456 StartAngle=1.5708 EndAngle=2.81984
    g4: GeomPoint [constr] X=30 Y=-47.3926 Z=0
    g5: ArcOfCircle CenterX=16 CenterY=-61.6754 CenterZ=0 NormalX=0 NormalY=0 NormalZ=1 AngleXU=0 Radius=20 StartAngle=0.795399 EndAngle=1.5708
    g6: LineSegment [constr] StartX=16 StartY=-41.6754 StartZ=0 EndX=16 EndY=-61.6754 EndZ=0
    g7: LineSegment [constr] StartX=16 StartY=-48 StartZ=0 EndX=10 EndY=-48 EndZ=0
  constraints (22):
    c: Vertical(g0)
    c: Coincident(g0,g1)
    c: Horizontal(g1)
    c: Coincident(g1,g2)
    c: Coincident(g1,g-3)
    c: Coincident(g5,g3)
    c: Coincident(g5,g2)
    c: Coincident(g6,g3)
    c: Coincident(g6,g5)
    c: Vertical(g6)
    c: PointOnObject(g3,g6)
    c: Vertical(g2)
    c: Coincident(g2,g4)
    c: Coincident(g0,g3)
    c: DistanceX(g0,g1) = 20
    c: DistanceY(g0,g0) = 6
    c: Radius(g5) = 20
    c: DistanceX(g3,g3) = 6
    c: Coincident(g7,g3)
    c: PointOnObject(g7,g0)
    c: Horizontal(g7)
    c: DistanceY(g0,g7) = 4
FEATURE [PartDesign::Pad] Pad012
  Direction = (0,0,1)
  Length = 37
  Length2 = 0
  Profile = -> Sketch047
  ReferenceAxis = -> Sketch047 [N_Axis]
  Refine = true
  Suppressed = false
  Type = 0
FEATURE [PartDesign::Plane] DatumPlane
  AttachmentOffset = pos=(0,0,-22) rot=(0,0,1;0rad)
  AttachmentSupport = -> [Pad012]
  Length = 68.2665
  MapMode = 5
  Placement = pos=(0,-30,-4.9e-15) rot=(1,0,0;1.5708rad)
  ResizeMode = 0
  Width = 93.2665
FEATURE [PartDesign::SubShapeBinder] Binder004  label="BasePlateBinder001"
  BindCopyOnChange = 0
  BindMode = 0
  ClaimChildren = false
  Context = -> Part017 [Body019.Binder004.]
  Fuse = false
  MakeFace = true
  OffsetFill = false
  OffsetIntersection = false
  OffsetJoinType = 0
  OffsetOpenResult = false
  PartialLoad = false
  Refine = true
  Relative = true
  Support = -> [Sketch]
  _Version = 2
FEATURE [Sketcher::SketchObject] Sketch048
  ArcFitTolerance = 1e-06
  AttachmentSupport = -> [Binder004]
  ExternalGeometry = -> [Binder004]
  FullyConstrained = true
  MakeInternals = false
  MapMode = 5
  Placement = pos=(0,0,0) rot=(1,0,0;1.5708rad)
  sketch-geometry (11):
    g0: LineSegment StartX=-30 StartY=-10 StartZ=0 EndX=-13 EndY=-10 EndZ=0
    g1: LineSegment StartX=-13 StartY=-10 StartZ=0 EndX=-13 EndY=-18 EndZ=0
    g2: LineSegment StartX=-13 StartY=-18 StartZ=0 EndX=13 EndY=-18 EndZ=0
    g3: LineSegment StartX=13 StartY=-18 StartZ=0 EndX=13 EndY=-10 EndZ=0
    g4: LineSegment StartX=13 StartY=-10 StartZ=0 EndX=30 EndY=-10 EndZ=0
    g5: LineSegment StartX=-30 StartY=-10 StartZ=0 EndX=-30 EndY=-14 EndZ=0
    g6: LineSegment StartX=-30 StartY=-14 StartZ=0 EndX=-19 EndY=-14 EndZ=0
    g7: LineSegment StartX=-19 StartY=-14 StartZ=0 EndX=-19 EndY=-22 EndZ=0
    g8: LineSegment StartX=-19 StartY=-22 StartZ=0 EndX=30 EndY=-22 EndZ=0
    g9: LineSegment [constr] StartX=-13 StartY=-10 StartZ=0 EndX=13 EndY=-10 EndZ=0
    g10: LineSegment StartX=30 StartY=-10 StartZ=0 EndX=30 EndY=-22 EndZ=0
  constraints (31):
    c: PointOnObject(g0,g-3)
    c: Horizontal(g0)
    c: Coincident(g0,g1)
    c: Vertical(g1)
    c: Coincident(g1,g2)
    c: Horizontal(g2)
    c: Coincident(g2,g3)
    c: Vertical(g3)
    c: Coincident(g3,g4)
    c: Horizontal(g4)
    c: Coincident(g0,g5)
    c: PointOnObject(g5,g-3)
    c: Coincident(g5,g6)
    c: Horizontal(g6)
    c: Coincident(g6,g7)
    c: Vertical(g7)
    c: Coincident(g7,g8)
    c: Horizontal(g8)
    c: DistanceY(g5,g5) = 4
    c: DistanceX(g6,g0) = 6
    c: Coincident(g9,g0)
    c: Coincident(g9,g3)
    c: DistanceY(g2,g-1) = 18
    c: Symmetric(g0,g3,g-2)
    c: DistanceY(g4,g-1) = 10
    c: DistanceY(g7,g1) = 4
    c: Coincident(g10,g4)
    c: Coincident(g10,g8)
    c: Vertical(g10)
    c: DistanceX(g2,g8) = 17
    c: DistanceX(g0,g-1) = 13
FEATURE [PartDesign::Pad] Pad013
  Direction = (0,-1,2e-16)
  Length = 52
  Length2 = 10
  Profile = -> Sketch048
  ReferenceAxis = -> Sketch048 [N_Axis]
  Refine = true
  Suppressed = false
  Type = 0
FEATURE [PartDesign::SubShapeBinder] Binder005  label="BackMountBinder002"
  BindCopyOnChange = 0
  BindMode = 0
  ClaimChildren = false
  Context = -> Part017 [Body020.Binder005.]
  Fuse = false
  MakeFace = true
  OffsetFill = false
  OffsetIntersection = false
  OffsetJoinType = 0
  OffsetOpenResult = false
  PartialLoad = false
  Refine = true
  Relative = true
  Support = -> [Sketch]
  _Version = 2
FEATURE [Sketcher::SketchObject] Sketch049
  ArcFitTolerance = 1e-06
  AttachmentSupport = -> [Binder005]
  ExternalGeometry = -> [Binder005]
  FullyConstrained = true
  MakeInternals = false
  MapMode = 5
  Placement = pos=(0,0,0) rot=(1,0,0;1.5708rad)
  sketch-geometry (8):
    g0: LineSegment StartX=-30 StartY=-9e-16 StartZ=0 EndX=-13 EndY=0 EndZ=0
    g1: LineSegment StartX=-13 StartY=0 StartZ=0 EndX=-13 EndY=-18 EndZ=0
    g2: LineSegment StartX=-13 StartY=-18 StartZ=0 EndX=13 EndY=-18 EndZ=0
    g3: LineSegment StartX=13 StartY=-18 StartZ=0 EndX=13 EndY=0 EndZ=0
    g4: LineSegment StartX=13 StartY=0 StartZ=0 EndX=30 EndY=-3.6e-15 EndZ=0
    g5: LineSegment StartX=30 StartY=-3.6e-15 StartZ=0 EndX=30 EndY=-55 EndZ=0
    g6: LineSegment StartX=30 StartY=-55 StartZ=0 EndX=-30 EndY=-55 EndZ=0
    g7: LineSegment StartX=-30 StartY=-55 StartZ=0 EndX=-30 EndY=0 EndZ=0
  constraints (22):
    c: Symmetric(g-3,g-3,g0)
    c: PointOnObject(g0,g-1)
    c: Coincident(g0,g1)
    c: Vertical(g1)
    c: Coincident(g1,g2)
    c: Horizontal(g2)
    c: Coincident(g2,g3)
    c: PointOnObject(g3,g-1)
    c: Vertical(g3)
    c: Coincident(g3,g4)
    c: Symmetric(g-4,g-4,g4)
    c: Coincident(g4,g5)
    c: PointOnObject(g5,g-4)
    c: Coincident(g5,g6)
    c: PointOnObject(g6,g-3)
    c: Horizontal(g6)
    c: Coincident(g6,g7)
    c: Coincident(g7,g0)
    c: Equal(g0,g4)
    c: DistanceY(g5,g5) = 55
    c: DistanceY(g3,g3) = 18
    c: DistanceX(g0,g0) = 17
FEATURE [PartDesign::Pad] Pad014
  Direction = (0,-1,2e-16)
  Length = 6
  Length2 = 10
  Profile = -> Sketch049
  ReferenceAxis = -> Sketch049 [N_Axis]
  Refine = true
  Suppressed = false
  Type = 0
FEATURE [PartDesign::Body] Body020  label="BackMount"
  AllowCompound = false
  Group = -> [Binder005,Sketch049,Pad014]
  Origin = -> Origin038
  Tip = -> Pad014
FEATURE [Sketcher::SketchObject] Sketch050
  ArcFitTolerance = 1e-06
  AttachmentOffset = pos=(0,0,49) rot=(0,0,1;0rad)
  AttachmentSupport = -> [XZ_Plane041]
  FullyConstrained = true
  MakeInternals = false
  MapMode = 5
  Placement = pos=(0,-49,1.09e-14) rot=(1,0,0;1.5708rad)
  sketch-geometry (19):
    g0: LineSegment StartX=-30 StartY=-10 StartZ=0 EndX=-13 EndY=-10 EndZ=0
    g1: LineSegment StartX=-13 StartY=-10 StartZ=0 EndX=-13 EndY=-21 EndZ=0
    g2: LineSegment StartX=-13 StartY=-21 StartZ=0 EndX=13 EndY=-21 EndZ=0
    g3: LineSegment StartX=13 StartY=-21 StartZ=0 EndX=13 EndY=-10 EndZ=0
    g4: LineSegment StartX=13 StartY=-10 StartZ=0 EndX=30 EndY=-10 EndZ=0
    g5: LineSegment StartX=30 StartY=-10 StartZ=0 EndX=30 EndY=-55 EndZ=0
    g6: LineSegment [constr] StartX=-13 StartY=-10 StartZ=0 EndX=13 EndY=-10 EndZ=0
    g7: LineSegment StartX=-13 StartY=-55 StartZ=0 EndX=-13 EndY=-44.5 EndZ=0
    g8: LineSegment StartX=-13 StartY=-44.5 StartZ=0 EndX=13 EndY=-44.5 EndZ=0
    g9: LineSegment StartX=13 StartY=-44.5 StartZ=0 EndX=13 EndY=-55 EndZ=0
    g10: LineSegment StartX=13 StartY=-55 StartZ=0 EndX=30 EndY=-55 EndZ=0
    g11: LineSegment [constr] StartX=-13 StartY=-21 StartZ=0 EndX=-13 EndY=-44.5 EndZ=0
    g12: LineSegment [constr] StartX=13 StartY=-21 StartZ=0 EndX=13 EndY=-44.5 EndZ=0
    g13: LineSegment StartX=-30 StartY=-10 StartZ=0 EndX=-30 EndY=-14 EndZ=0
    g14: LineSegment StartX=-30 StartY=-14 StartZ=0 EndX=-25 EndY=-14 EndZ=0
    g15: LineSegment StartX=-25 StartY=-14 StartZ=0 EndX=-25 EndY=-55 EndZ=0
    g16: LineSegment [constr] StartX=-30 StartY=-14 StartZ=0 EndX=-30 EndY=-55 EndZ=0
    g17: LineSegment StartX=-25 StartY=-55 StartZ=0 EndX=-13 EndY=-55 EndZ=0
    g18: LineSegment [constr] StartX=-25 StartY=-55 StartZ=0 EndX=-30 EndY=-55 EndZ=0
  constraints (51):
    c: Horizontal(g0)
    c: Coincident(g0,g1)
    c: Vertical(g1)
    c: Coincident(g1,g2)
    c: Horizontal(g2)
    c: Coincident(g2,g3)
    c: Vertical(g3)
    c: Coincident(g3,g4)
    c: Horizontal(g4)
    c: Coincident(g4,g5)
    c: Vertical(g5)
    c: DistanceX(g2,g2) = 26
    c: DistanceY(g16,g-1) = 55
    c: Coincident(g6,g0)
    c: Coincident(g6,g3)
    c: Symmetric(g0,g3,g-2)
    c: DistanceX(g16,g5) = 60
    c: DistanceY(g1,g1) = 11
    c: Symmetric(g16,g5,g-2)
    c: Vertical(g7)
    c: Coincident(g7,g8)
    c: Horizontal(g8)
    c: Coincident(g8,g9)
    c: Vertical(g9)
    c: Coincident(g9,g10)
    c: Coincident(g10,g5)
    c: Horizontal(g10)
    c: Coincident(g11,g1)
    c: Coincident(g11,g7)
    c: Vertical(g11)
    c: Coincident(g12,g2)
    c: Coincident(g12,g8)
    c: Vertical(g12)
    c: DistanceY(g9,g9) = 10.5
    c: Coincident(g0,g13)
    c: Coincident(g13,g14)
    c: Horizontal(g14)
    c: Coincident(g14,g15)
    c: Vertical(g15)
    c: DistanceX(g14,g14) = 5
    c: Coincident(g16,g13)
    c: Vertical(g16)
    c: Vertical(g13)
    c: Coincident(g17,g15)
    c: Coincident(g17,g7)
    c: Horizontal(g17)
    c: Coincident(g18,g15)
    c: Coincident(g18,g16)
    c: Horizontal(g18)
    c: DistanceY(g13,g-1) = 14
    c: DistanceY(g13,g0) = 4
FEATURE [PartDesign::Pad] Pad015
  Direction = (0,-1,2e-16)
  Length = 5
  Length2 = 10
  Placement = pos=(0,0,0) rot=(1,0,0;1.5708rad)
  Profile = -> Sketch050
  ReferenceAxis = -> Sketch050 [N_Axis]
  Refine = true
  Suppressed = false
  Type = 0
FEATURE [PartDesign::SubShapeBinder] Binder006  label="CoolingFanBaseBinder"
  BindCopyOnChange = 0
  BindMode = 0
  ClaimChildren = false
  Context = -> Part017 [Body025.Binder006.]
  Fuse = false
  MakeFace = true
  OffsetFill = false
  OffsetIntersection = false
  OffsetJoinType = 0
  OffsetOpenResult = false
  PartialLoad = false
  Refine = true
  Relative = true
  _Version = 2
FEATURE [PartDesign::Plane] DatumPlane001
  AttachmentSupport = -> [Binder006]
  Length = 92.6971
  MapMode = 45
  Placement = pos=(-25,-46,-34.5) rot=(0.57735,0.57735,0.57735;2.0944rad)
  ResizeMode = 0
  Width = 95.6971
FEATURE [PartDesign::SubShapeBinder] Binder007  label="MountingPlateBinder002"
  BindCopyOnChange = 0
  BindMode = 0
  ClaimChildren = false
  Context = -> Part017 [Body025.Binder007.]
  Fuse = false
  MakeFace = true
  OffsetFill = false
  OffsetIntersection = false
  OffsetJoinType = 0
  OffsetOpenResult = false
  PartialLoad = false
  Refine = true
  Relative = true
  Support = -> [Sketch]
  _Version = 2
FEATURE [Sketcher::SketchObject] Sketch054
  ArcFitTolerance = 1e-06
  AttachmentSupport = -> [DatumPlane001]
  ExternalGeometry = -> [Binder006,Binder007]
  FullyConstrained = false
  MakeInternals = false
  MapMode = 5
  Placement = pos=(-25,-46,-34.5) rot=(0.57735,-0.57735,-0.57735;2.0944rad)
  sketch-geometry (6):
    g0: LineSegment StartX=6 StartY=-20.5 StartZ=0 EndX=6 EndY=24.5 EndZ=0
    g1: LineSegment StartX=6 StartY=24.5 StartZ=0 EndX=-40 EndY=24.5 EndZ=0
    g2: LineSegment StartX=-40 StartY=24.5 StartZ=0 EndX=-40 EndY=-20.5 EndZ=0
    g3: LineSegment StartX=-40 StartY=-20.5 StartZ=0 EndX=6 EndY=-20.5 EndZ=0
    g4: LineSegment [constr] StartX=-46 StartY=-20.5 StartZ=0 EndX=-40 EndY=-20.5 EndZ=0
    g5: Circle [constr] CenterX=-15.857 CenterY=-1.12972 CenterZ=0 NormalX=0 NormalY=0 NormalZ=1 AngleXU=0 Radius=10.6353
  constraints (14):
    c: Coincident(g0,g1)
    c: Coincident(g1,g2)
    c: Coincident(g2,g3)
    c: Coincident(g3,g0)
    c: Vertical(g0)
    c: Vertical(g2)
    c: Horizontal(g1)
    c: Horizontal(g3)
    c: Coincident(g4,g-5)
    c: Coincident(g4,g2)
    c: Horizontal(g4)
    c: DistanceY(g0,g0) = 45
    c: DistanceX(g1,g1) = 46
    c: DistanceX(g4,g4) = 6
FEATURE [PartDesign::Pad] Pad019  label="HeatBreakCoolingBody"
  Direction = (-1,-7.52e-14,-1e-16)
  Length = 6
  Length2 = 0
  Placement = pos=(-25,-46,-34.5) rot=(0.57735,0.57735,0.57735;2.0944rad)
  Profile = -> Sketch054
  ReferenceAxis = -> Sketch054 [N_Axis]
  Refine = true
  Reversed = true
  Suppressed = false
  Type = 0
FEATURE [Sketcher::SketchObject] Sketch057
  ArcFitTolerance = 1e-06
  AttachmentSupport = -> [Pad012]
  ExternalGeometry = -> [Pad012,DatumPlane]
  FullyConstrained = true
  MakeInternals = false
  MapMode = 5
  Placement = pos=(0,0,-55) rot=(1,0,0;3.14159rad)
  sketch-geometry (4):
    g0: LineSegment StartX=20 StartY=52 StartZ=0 EndX=30 EndY=52 EndZ=0
    g1: LineSegment StartX=30 StartY=52 StartZ=0 EndX=30 EndY=30 EndZ=0
    g2: LineSegment StartX=30 StartY=30 StartZ=0 EndX=20 EndY=30 EndZ=0
    g3: LineSegment StartX=20 StartY=30 StartZ=0 EndX=20 EndY=52 EndZ=0
  constraints (11):
    c: Coincident(g0,g1)
    c: Coincident(g1,g2)
    c: Coincident(g2,g3)
    c: Coincident(g3,g0)
    c: Horizontal(g0)
    c: Horizontal(g2)
    c: Vertical(g1)
    c: Vertical(g3)
    c: Coincident(g0,g-3)
    c: DistanceX(g0,g0) = 10
    c: PointOnObject(g1,g-4)
FEATURE [PartDesign::Pad] Pad020
  BaseFeature = -> Pad012
  Direction = (0,0,-1)
  Length = 2
  Length2 = 10
  Profile = -> Sketch057
  ReferenceAxis = -> Sketch057 [N_Axis]
  Refine = true
  Reversed = true
  Suppressed = false
  Type = 0
FEATURE [PartDesign::Mirrored] Mirrored
  BaseFeature = -> Pad020
  MirrorPlane = -> DatumPlane
  Originals = -> [Pad020,Pad012]
  Refine = true
  Suppressed = false
  TransformMode = 0
FEATURE [PartDesign::Pad] Pad021
  BaseFeature = -> Mirrored
  Direction = (0,1,-4e-16)
  Length = 2
  Length2 = 10
  Profile = -> Mirrored [Face14]
  Refine = true
  Suppressed = false
  Type = 0
FEATURE [PartDesign::Body] Body018  label="ExhaustSide"
  AllowCompound = false
  Group = -> [Binder003,Sketch047,Pad012,DatumPlane,Sketch057,Pad020,Mirrored,Pad021]
  Origin = -> Origin036
  Tip = -> Pad021
FEATURE [Sketcher::SketchObject] Sketch061  label="FanDuctSk"
  ArcFitTolerance = 1e-06
  AttachmentSupport = -> [Pad019]
  ExternalGeometry = -> [Binder006]
  FullyConstrained = true
  MakeInternals = false
  MapMode = 5
  Placement = pos=(-25,-46,-34.5) rot=(0.57735,0.57735,-0.57735;4.18879rad)
  sketch-geometry (2):
    g0: Circle CenterX=16 CenterY=-5e-16 CenterZ=0 NormalX=0 NormalY=0 NormalZ=1 AngleXU=0 Radius=19
    g1: LineSegment [constr] StartX=2.13e-14 StartY=16 StartZ=0 EndX=32 EndY=-16 EndZ=0
  constraints (4):
    c: Diameter(g0) = 38
    c: Coincident(g1,g-3)
    c: Coincident(g1,g-4)
    c: Symmetric(g1,g1,g0)
FEATURE [PartDesign::Pocket] Pocket026  label="FanDuctPk"
  BaseFeature = -> Pad019
  Direction = (1,7.51e-14,0)
  Length = 6
  Length2 = 5
  Placement = pos=(-25,-46,-34.5) rot=(0.57735,0.57735,0.57735;2.0944rad)
  Profile = -> Sketch061
  ReferenceAxis = -> Sketch061 [N_Axis]
  Refine = true
  Suppressed = false
  Type = 0
FEATURE [PartDesign::Body] Body025  label="HeatBreakFanMount"
  AllowCompound = false
  Group = -> [Binder006,DatumPlane001,Binder007,Sketch054,Pad019,Sketch061,Pocket026]
  Origin = -> Origin043
  Tip = -> Pocket026
FEATURE [Sketcher::SketchObject] Sketch063
  ArcFitTolerance = 1e-06
  AttachmentSupport = -> [Pad013]
  FullyConstrained = true
  MakeInternals = false
  MapMode = 5
  Placement = pos=(0,-4e-15,-18) rot=(0,0,1;0rad)
  sketch-geometry (1):
    g0: Circle CenterX=0 CenterY=-30 CenterZ=0 NormalX=0 NormalY=0 NormalZ=1 AngleXU=0 Radius=12.5
  constraints (3):
    c: PointOnObject(g0,g-2)
    c: Diameter(g0) = 25
    c: DistanceY(g0,g-1) = 30
FEATURE [PartDesign::Pocket] Pocket027
  BaseFeature = -> Pad013
  Direction = (0,0,-1)
  Length = 5
  Length2 = 5
  Profile = -> Sketch063
  ReferenceAxis = -> Sketch063 [N_Axis]
  Refine = true
  Suppressed = false
  Type = 0
FEATURE [Sketcher::SketchObject] Sketch064
  ArcFitTolerance = 1e-06
  AttachmentSupport = -> [Pocket027]
  FullyConstrained = true
  MakeInternals = false
  MapMode = 5
  Placement = pos=(0,-4e-15,-18) rot=(0,0,1;0rad)
  sketch-geometry (4):
    g0: LineSegment StartX=-3 StartY=-6 StartZ=0 EndX=-3 EndY=-49 EndZ=0
    g1: LineSegment StartX=-3 StartY=-49 StartZ=0 EndX=3 EndY=-49 EndZ=0
    g2: LineSegment StartX=3 StartY=-49 StartZ=0 EndX=3 EndY=-6 EndZ=0
    g3: LineSegment StartX=3 StartY=-6 StartZ=0 EndX=-3 EndY=-6 EndZ=0
  constraints (11):
    c: Coincident(g0,g1)
    c: Coincident(g1,g2)
    c: Coincident(g2,g3)
    c: Coincident(g3,g0)
    c: Vertical(g0)
    c: Vertical(g2)
    c: Horizontal(g1)
    c: DistanceY(g2,g-1) = 6
    c: DistanceX(g1,g1) = 6
    c: DistanceY(g0,g0) = 43
    c: Symmetric(g0,g2,g-2)
FEATURE [PartDesign::Pocket] Pocket028
  BaseFeature = -> Pocket027
  Direction = (0,0,-1)
  Length = 5
  Length2 = 5
  Profile = -> Sketch064
  ReferenceAxis = -> Sketch064 [N_Axis]
  Refine = true
  Suppressed = false
  Type = 0
FEATURE [Sketcher::SketchObject] Sketch065
  ArcFitTolerance = 1e-06
  AttachmentSupport = -> [Pad015]
  FullyConstrained = true
  MakeInternals = false
  MapMode = 5
  Placement = pos=(0,-54,1.57e-14) rot=(1,0,0;1.5708rad)
FEATURE [PartDesign::SubShapeBinder] Binder008
  BindCopyOnChange = 0
  BindMode = 0
  ClaimChildren = false
  Context = -> Part017 [Body023.Binder008.]
  Fuse = false
  MakeFace = true
  OffsetFill = false
  OffsetIntersection = false
  OffsetJoinType = 0
  OffsetOpenResult = false
  PartialLoad = false
  Refine = true
  Relative = true
  Support = -> [Sketch046]
  _Version = 2
FEATURE [Sketcher::SketchObject] Sketch066  label="FrontMountBosses Sk"
  ArcFitTolerance = 1e-06
  AttachmentOffset = pos=(0,0,2) rot=(0,0,1;0rad)
  AttachmentSupport = -> [Pad015]
  ExternalGeometry = -> [Binder008,Pad015]
  FullyConstrained = true
  MakeInternals = false
  MapMode = 5
  Placement = pos=(0,-56,1.61e-14) rot=(1,0,0;1.5708rad)
  sketch-geometry (20):
    g0: Circle [constr] CenterX=19 CenterY=-49.5 CenterZ=0 NormalX=0 NormalY=0 NormalZ=1 AngleXU=0 Radius=4
    g1: LineSegment StartX=15 StartY=-51.8094 StartZ=0 EndX=19 EndY=-54.1188 EndZ=0
    g2: LineSegment StartX=19 StartY=-54.1188 StartZ=0 EndX=23 EndY=-51.8094 EndZ=0
    g3: LineSegment StartX=23 StartY=-51.8094 StartZ=0 EndX=23 EndY=-47.1906 EndZ=0
    g4: LineSegment StartX=23 StartY=-47.1906 StartZ=0 EndX=19 EndY=-44.8812 EndZ=0
    g5: LineSegment StartX=19 StartY=-44.8812 StartZ=0 EndX=15 EndY=-47.1906 EndZ=0
    g6: LineSegment StartX=15 StartY=-47.1906 StartZ=0 EndX=15 EndY=-51.8094 EndZ=0
    g7: LineSegment StartX=-30 StartY=-10 StartZ=0 EndX=-24 EndY=-6.5359 EndZ=0
    g8: LineSegment StartX=-24 StartY=-6.5359 StartZ=0 EndX=-18 EndY=-10 EndZ=0
    g9: LineSegment [constr] StartX=-30 StartY=-10 StartZ=0 EndX=-18 EndY=-10 EndZ=0
    g10: LineSegment [constr] StartX=-24 StartY=-6.5359 StartZ=0 EndX=-24 EndY=-11.5 EndZ=0
    g11: LineSegment StartX=-30 StartY=-10 StartZ=0 EndX=-30 EndY=-14 EndZ=0
    g12: LineSegment [constr] StartX=-30 StartY=-14 StartZ=0 EndX=-24 EndY=-17.4641 EndZ=0
    g13: LineSegment StartX=-24 StartY=-17.4641 StartZ=0 EndX=-18 EndY=-14 EndZ=0
    g14: LineSegment [constr] StartX=-24 StartY=-11.5 StartZ=0 EndX=-24 EndY=-17.4641 EndZ=0
    g15: LineSegment StartX=-18 StartY=-14 StartZ=0 EndX=-18 EndY=-10 EndZ=0
    g16: LineSegment [constr] StartX=-30 StartY=-14 StartZ=0 EndX=-18 EndY=-14 EndZ=0
    g17: LineSegment StartX=-30 StartY=-14 StartZ=0 EndX=-30 EndY=-55 EndZ=0
    g18: LineSegment StartX=-30 StartY=-55 StartZ=0 EndX=-24 EndY=-55 EndZ=0
    g19: LineSegment StartX=-24 StartY=-55 StartZ=0 EndX=-24 EndY=-17.4641 EndZ=0
  constraints (47):
    c: Diameter(g0) = 8
    c: Coincident(g0,g-4)
    c: Coincident(g1,g2)
    c: Coincident(g2,g3)
    c: Coincident(g3,g4)
    c: Coincident(g4,g5)
    c: Coincident(g5,g6)
    c: Coincident(g6,g1)
    c: Equal(g1, g2-g6) x5
    c: Tangent(g6,g0)
    c: Vertical(g6)
    c: Tangent(g3,g0)
    c: Tangent(g4,g0)
    c: Tangent(g5,g0)
    c: Tangent(g0,g1)
    c: Angle(g6,g5) = 2.0944
    c: Coincident(g7,g8)
    c: Coincident(g9,g7)
    c: Coincident(g9,g8)
    c: Horizontal(g9)
    c: Coincident(g10,g7)
    c: Vertical(g10)
    c: Coincident(g7,g11)
    c: Coincident(g11,g12)
    c: Coincident(g12,g13)
    c: Coincident(g14,g12)
    c: Coincident(g15,g13)
    c: Coincident(g15,g8)
    c: Vertical(g15)
    c: Angle(g13,g12) = 2.0944
    c: Coincident(g10,g14)
    c: Coincident(g10,g-3)
    c: Coincident(g11,g-5)
    c: Symmetric(g7,g8,g14)
    c: Coincident(g7,g-5)
    c: Coincident(g16,g11)
    c: Coincident(g16,g13)
    c: Horizontal(g16)
    c: Angle(g7,g8) = 2.0944
    c: Coincident(g17,g11)
    c: Vertical(g17)
    c: Coincident(g18,g17)
    c: PointOnObject(g18,g-6)
    c: Horizontal(g18)
    c: Coincident(g19,g18)
    c: Coincident(g19,g12)
    c: Vertical(g19)
FEATURE [PartDesign::Pad] Pad023  label="FrontMountBosses"
  BaseFeature = -> Pad015
  Direction = (0,-1,2e-16)
  Length = 5
  Length2 = 10
  Placement = pos=(0,0,0) rot=(1,0,0;1.5708rad)
  Profile = -> Sketch066
  ReferenceAxis = -> Sketch066 [N_Axis]
  Refine = true
  Reversed = true
  Suppressed = false
  Type = 0
FEATURE [PartDesign::Body] Body023  label="FrontMount"
  AllowCompound = false
  Group = -> [Sketch050,Pad015,Sketch065,Binder008,Sketch066,Pad023]
  Origin = -> Origin041
  Tip = -> Pad023
FEATURE [PartDesign::SubShapeBinder] Binder010  label="CoolingFanMountBinder"
  BindCopyOnChange = 0
  BindMode = 0
  ClaimChildren = false
  Context = -> Part017 [Body025.Binder010.]
  Fuse = false
  MakeFace = true
  OffsetFill = false
  OffsetIntersection = false
  OffsetJoinType = 0
  OffsetOpenResult = false
  PartialLoad = false
  Placement = pos=(0,-4,0) rot=(0,0,1;0rad)
  Refine = true
  Relative = true
  Support = -> [Sketch046]
  _Version = 2
FEATURE [PartDesign::SubShapeBinder] Binder011  label="BaseMountHolesBinder"
  BindCopyOnChange = 0
  BindMode = 0
  ClaimChildren = false
  Context = -> Part017 [Body025.Binder011.]
  Fuse = false
  MakeFace = true
  OffsetFill = false
  OffsetIntersection = false
  OffsetJoinType = 0
  OffsetOpenResult = false
  PartialLoad = false
  Placement = pos=(0,-18.5,0) rot=(0,0,1;0rad)
  Refine = true
  Relative = true
  Support = -> [Sketch[Edge12,Edge11,Edge16,Edge15]]
  _Version = 2
FEATURE [PartDesign::FeatureBase] Clone009
  BaseFeature = -> Body025
  Suppressed = false
FEATURE [PartDesign::Body] Body027  label="HeatBreakFanMountClone"
  AllowCompound = false
  Group = -> [Clone009]
  Origin = -> Origin046
  Tip = -> Clone009
FEATURE [PartDesign::FeatureBase] Clone010
  BaseFeature = -> Body018
  Suppressed = false
FEATURE [PartDesign::Body] Body028  label="ExhaustSideClone"
  AllowCompound = false
  Group = -> [Clone010]
  Origin = -> Origin047
  Tip = -> Clone010
FEATURE [Sketcher::SketchObject] Sketch071
  ArcFitTolerance = 1e-06
  AttachmentSupport = -> [Pocket028]
  ExternalGeometry = -> [Pocket028]
  FullyConstrained = true
  MakeInternals = false
  MapMode = 5
  Placement = pos=(-30,0,0) rot=(0.57735,-0.57735,-0.57735;2.0944rad)
  expr: Constraints[10] = <<Properties>>.M3Inset
  sketch-geometry (8):
    g0: LineSegment StartX=52 StartY=-10 StartZ=0 EndX=52 EndY=0 EndZ=0
    g1: LineSegment StartX=52 StartY=0 StartZ=0 EndX=36 EndY=0 EndZ=0
    g2: LineSegment StartX=36 StartY=0 StartZ=0 EndX=36 EndY=-10 EndZ=0
    g3: LineSegment StartX=36 StartY=-10 StartZ=0 EndX=52 EndY=-10 EndZ=0
    g4: Circle CenterX=44 CenterY=-5 CenterZ=0 NormalX=0 NormalY=0 NormalZ=1 AngleXU=0 Radius=2.75
    g5: LineSegment [constr] StartX=36 StartY=-5 StartZ=0 EndX=52 EndY=-5 EndZ=0
    g6: LineSegment [constr] StartX=0 StartY=0 StartZ=0 EndX=36 EndY=0 EndZ=0
    g7: LineSegment [constr] StartX=44 StartY=0 StartZ=0 EndX=44 EndY=-5 EndZ=0
  constraints (20):
    c: Coincident(g0,g1)
    c: Coincident(g1,g2)
    c: Coincident(g2,g3)
    c: Coincident(g3,g0)
    c: Vertical(g0)
    c: Vertical(g2)
    c: Horizontal(g1)
    c: Horizontal(g3)
    c: Distance(g0,g2) = 16
    c: Coincident(g0,g-3)
    c: Diameter(g4) = 5.5
    c: Symmetric(g2,g2,g5)
    c: Symmetric(g0,g0,g5)
    c: PointOnObject(g4,g5)
    c: Coincident(g6,g-1)
    c: Coincident(g6,g1)
    c: Horizontal(g6)
    c: Symmetric(g1,g1,g7)
    c: Coincident(g7,g4)
    c: Vertical(g7)
FEATURE [PartDesign::Pad] Pad026  label="LeftCoverTab"
  BaseFeature = -> Pocket028
  Direction = (-1,0,0)
  Length = 4
  Length2 = 10
  Profile = -> Sketch071
  ReferenceAxis = -> Sketch071 [N_Axis]
  Refine = true
  Reversed = true
  Suppressed = false
  Type = 0
FEATURE [Sketcher::SketchObject] Sketch072
  ArcFitTolerance = 1e-06
  AttachmentSupport = -> [Pad026]
  ExternalGeometry = -> [Pad026]
  FullyConstrained = true
  MakeInternals = false
  MapMode = 5
  Placement = pos=(30,0,0) rot=(0.57735,0.57735,0.57735;2.0944rad)
  expr: Constraints[18] = <<Properties>>.M3Inset
  sketch-geometry (7):
    g0: LineSegment StartX=-52 StartY=-10 StartZ=0 EndX=-36 EndY=-10 EndZ=0
    g1: LineSegment StartX=-36 StartY=-10 StartZ=0 EndX=-36 EndY=0 EndZ=0
    g2: LineSegment StartX=-36 StartY=0 StartZ=0 EndX=-52 EndY=0 EndZ=0
    g3: LineSegment StartX=-52 StartY=0 StartZ=0 EndX=-52 EndY=-10 EndZ=0
    g4: LineSegment [constr] StartX=-36 StartY=0 StartZ=0 EndX=0 EndY=0 EndZ=0
    g5: LineSegment [constr] StartX=-52 StartY=-5 StartZ=0 EndX=-36 EndY=-5 EndZ=0
    g6: Circle CenterX=-44 CenterY=-5 CenterZ=0 NormalX=0 NormalY=0 NormalZ=1 AngleXU=0 Radius=2.75
  constraints (19):
    c: Coincident(g0,g1)
    c: Coincident(g1,g2)
    c: Coincident(g2,g3)
    c: Coincident(g3,g0)
    c: Horizontal(g0)
    c: Horizontal(g2)
    c: Vertical(g1)
    c: Vertical(g3)
    c: Distance(g1,g3) = 16
    c: Coincident(g0,g-3)
    c: Coincident(g4,g1)
    c: Coincident(g4,g-1)
    c: Horizontal(g4)
    c: PointOnObject(g5,g3)
    c: Symmetric(g1,g1,g5)
    c: Horizontal(g5)
    c: PointOnObject(g6,g5)
    c: DistanceX(g6,g1) = 8
    c: Diameter(g6) = 5.5
FEATURE [PartDesign::Pad] Pad027  label="RightCoverTab"
  BaseFeature = -> Pad026
  Direction = (1,0,0)
  Length = 4
  Length2 = 10
  Profile = -> Sketch072
  ReferenceAxis = -> Sketch072 [N_Axis]
  Refine = true
  Reversed = true
  Suppressed = false
  Type = 0
FEATURE [PartDesign::Body] Body019  label="TopMount"
  AllowCompound = false
  Group = -> [Binder004,Sketch048,Pad013,Sketch063,Pocket027,Sketch064,Pocket028,Sketch071,Pad026,Sketch072,Pad027]
  Origin = -> Origin037
  Tip = -> Pad027
FEATURE [App::Part] Part017  label="ToolBodies"
  Group = -> [Body025,Body018,Body019,Body020,Body023]
  Origin = -> Origin035
FEATURE [PartDesign::FeatureBase] Clone011
  BaseFeature = -> Body019
  Suppressed = false
FEATURE [PartDesign::Body] Body029  label="TopMountClone"
  AllowCompound = false
  Group = -> [Clone011]
  Origin = -> Origin048
  Tip = -> Clone011
FEATURE [PartDesign::FeatureBase] Clone012
  BaseFeature = -> Body020
  Suppressed = false
FEATURE [PartDesign::Body] Body030  label="BackMountClone"
  AllowCompound = false
  Group = -> [Clone012]
  Origin = -> Origin049
  Tip = -> Clone012
FEATURE [PartDesign::FeatureBase] Clone013
  BaseFeature = -> Body023
  Suppressed = false
FEATURE [PartDesign::Body] Body031  label="FrontMountClone"
  AllowCompound = false
  Group = -> [Clone013]
  Origin = -> Origin050
  Tip = -> Clone013
FEATURE [PartDesign::Boolean] Boolean
  Group = -> [Body031,Body028,Body027,Body030,Body029]
  Refine = true
  Suppressed = false
  Type = 0
  UsePlacement = true
FEATURE [Sketcher::SketchObject] Sketch070  label="CoolingFanClearance"
  ArcFitTolerance = 1e-06
  AttachmentSupport = -> [Boolean]
  FullyConstrained = true
  MakeInternals = false
  MapMode = 5
  Placement = pos=(-1.067e-13,-6,-2.9e-15) rot=(1,0,0;1.5708rad)
  sketch-geometry (4):
    g0: LineSegment StartX=-19 StartY=-22 StartZ=0 EndX=-13 EndY=-22 EndZ=0
    g1: LineSegment StartX=-13 StartY=-22 StartZ=0 EndX=-18.5 EndY=-16.5 EndZ=0
    g2: LineSegment StartX=-18.5 StartY=-16.5 StartZ=0 EndX=-19 EndY=-16.5 EndZ=0
    g3: LineSegment StartX=-19 StartY=-16.5 StartZ=0 EndX=-19 EndY=-22 EndZ=0
  constraints (12):
    c: Horizontal(g0)
    c: Coincident(g0,g1)
    c: Coincident(g1,g2)
    c: Horizontal(g2)
    c: Coincident(g2,g3)
    c: Coincident(g3,g0)
    c: Vertical(g3)
    c: Angle(g1,g0) = 0.785398
    c: DistanceX(g0,g-1) = 13
    c: DistanceY(g0,g-1) = 22
    c: DistanceX(g0,g0) = 6
    c: DistanceY(g3,g3) = 5.5
FEATURE [PartDesign::Pocket] Pocket029
  BaseFeature = -> Boolean
  Direction = (1.78e-14,1,-2e-16)
  Length = 0
  Length2 = 5
  Profile = -> Sketch070
  ReferenceAxis = -> Sketch070 [N_Axis]
  Refine = true
  Reversed = true
  Suppressed = false
  Type = 3
  UpToFace = -> Boolean [Face66]
FEATURE [PartDesign::Pad] Pad028
  BaseFeature = -> Pocket029
  Direction = (0,-1,0)
  Length = 10
  Length2 = 10
  Profile = -> Pocket029 [Face7]
  Refine = true
  Suppressed = false
  Type = 3
  UpToFace = -> Pocket029 [Face9]
FEATURE [PartDesign::Pocket] Pocket030  label="LowerBridgeCutout Pk"
  BaseFeature = -> Pad028
  Direction = (0,1,0)
  Length = 0
  Length2 = 5
  Profile = -> Pad028 [Face35]
  Refine = true
  Suppressed = false
  Type = 3
  UpToFace = -> Pad028 [Face27]
FEATURE [PartDesign::SubShapeBinder] Binder012  label="MountPlateBinder"
  BindCopyOnChange = 0
  BindMode = 0
  ClaimChildren = false
  Context = -> Part018 [Body026.Binder012.]
  Fuse = false
  MakeFace = true
  OffsetFill = false
  OffsetIntersection = false
  OffsetJoinType = 0
  OffsetOpenResult = false
  PartialLoad = false
  Refine = true
  Relative = true
  Support = -> [Sketch045]
  _Version = 2
FEATURE [PartDesign::SubShapeBinder] Binder013  label="CoolingDuctBinder"
  BindCopyOnChange = 0
  BindMode = 0
  ClaimChildren = false
  Context = -> Part018 [Body026.Binder013.]
  Fuse = false
  MakeFace = true
  OffsetFill = false
  OffsetIntersection = false
  OffsetJoinType = 0
  OffsetOpenResult = false
  PartialLoad = false
  Refine = true
  Relative = true
  Support = -> [Sketch042]
  _Version = 2
FEATURE [Sketcher::SketchObject] Sketch073  label="CoolingDuctBosses"
  ArcFitTolerance = 1e-06
  AttachmentSupport = -> [Boolean]
  ExternalGeometry = -> [Binder013]
  FullyConstrained = true
  MakeInternals = false
  MapMode = 5
  Placement = pos=(0,-1.89e-14,-55) rot=(1,0,0;3.14159rad)
  sketch-geometry (14):
    g0: LineSegment StartX=-19 StartY=43.3812 StartZ=0 EndX=-15 EndY=45.6906 EndZ=0
    g1: LineSegment StartX=-15 StartY=45.6906 StartZ=0 EndX=-15 EndY=50.3094 EndZ=0
    g2: LineSegment StartX=-15 StartY=50.3094 StartZ=0 EndX=-19 EndY=52.6188 EndZ=0
    g3: LineSegment StartX=-19 StartY=52.6188 StartZ=0 EndX=-23 EndY=50.3094 EndZ=0
    g4: LineSegment StartX=-23 StartY=50.3094 StartZ=0 EndX=-23 EndY=45.6906 EndZ=0
    g5: LineSegment StartX=-23 StartY=45.6906 StartZ=0 EndX=-19 EndY=43.3812 EndZ=0
    g6: Circle [constr] CenterX=-19 CenterY=48 CenterZ=0 NormalX=0 NormalY=0 NormalZ=1 AngleXU=0 Radius=4.6188
    g7: LineSegment StartX=-15 StartY=3.6906 StartZ=0 EndX=-15 EndY=8.3094 EndZ=0
    g8: LineSegment StartX=-15 StartY=8.3094 StartZ=0 EndX=-19 EndY=10.6188 EndZ=0
    g9: LineSegment StartX=-19 StartY=10.6188 StartZ=0 EndX=-23 EndY=8.3094 EndZ=0
    g10: LineSegment StartX=-23 StartY=8.3094 StartZ=0 EndX=-23 EndY=3.6906 EndZ=0
    g11: LineSegment StartX=-23 StartY=3.6906 StartZ=0 EndX=-19 EndY=1.3812 EndZ=0
    g12: LineSegment StartX=-19 StartY=1.3812 StartZ=0 EndX=-15 EndY=3.6906 EndZ=0
    g13: Circle [constr] CenterX=-19 CenterY=6 CenterZ=0 NormalX=0 NormalY=0 NormalZ=1 AngleXU=0 Radius=4.6188
  constraints (32):
    c: Coincident(g0,g1)
    c: Coincident(g1,g2)
    c: Coincident(g2,g3)
    c: Coincident(g3,g4)
    c: Coincident(g4,g5)
    c: Coincident(g5,g0)
    c: Equal(g0, g1-g5) x5
    c: PointOnObject(g0,g6)
    c: PointOnObject(g1,g6)
    c: PointOnObject(g2,g6)
    c: PointOnObject(g3,g6)
    c: PointOnObject(g4,g6)
    c: PointOnObject(g5,g6)
    c: Coincident(g6,g-3)
    c: Coincident(g7,g8)
    c: Coincident(g8,g9)
    c: Coincident(g9,g10)
    c: Coincident(g10,g11)
    c: Coincident(g11,g12)
    c: Coincident(g12,g7)
    c: Equal(g7, g8-g12) x5
    c: PointOnObject(g7,g13)
    c: PointOnObject(g8,g13)
    c: PointOnObject(g9,g13)
    c: PointOnObject(g10,g13)
    c: PointOnObject(g11,g13)
    c: PointOnObject(g12,g13)
    c: Coincident(g13,g-4)
    c: Vertical(g7)
    c: Vertical(g1)
    c: DistanceX(g9,g7) = 8
    c: DistanceX(g4,g0) = 8
FEATURE [PartDesign::Pad] Pad029
  BaseFeature = -> Pocket030
  Direction = (0,0,-1)
  Length = 5
  Length2 = 10
  Profile = -> Sketch073
  ReferenceAxis = -> Sketch073 [N_Axis]
  Refine = true
  Reversed = true
  Suppressed = false
  Type = 0
FEATURE [PartDesign::Pocket] Pocket031  label="HotEndFanFace"
  BaseFeature = -> Pad029
  Direction = (1,7.05e-14,0)
  Length = 1
  Length2 = 5
  Profile = -> Pad029 [Face36]
  Refine = true
  Suppressed = false
  Type = 0
FEATURE [PartDesign::Pocket] Pocket032  label="CoolingDuctInsets"
  BaseFeature = -> Pocket031
  Direction = (0,0,-1)
  Length = 4
  Length2 = 5
  Profile = -> Binder013
  Refine = true
  Reversed = true
  Suppressed = false
  Type = 0
FEATURE [PartDesign::Pocket] Pocket033  label="CoolingFanInsets"
  BaseFeature = -> Pocket032
  Direction = (0,-1,3e-16)
  Length = 4
  Length2 = 5
  Profile = -> Binder010
  Refine = true
  Reversed = true
  Suppressed = false
  Type = 0
FEATURE [Sketcher::SketchObject] Sketch074  label="HeatBreakCableGuideSk"
  ArcFitTolerance = 1e-06
  FullyConstrained = true
  MakeInternals = false
  MapMode = 5
  Placement = pos=(0,-3.6e-15,-14) rot=(1,0,0;3.14159rad)
  sketch-geometry (6):
    g0: LineSegment StartX=-30 StartY=14 StartZ=0 EndX=-24 EndY=14 EndZ=0
    g1: LineSegment StartX=-24 StartY=14 StartZ=0 EndX=-24 EndY=19 EndZ=0
    g2: LineSegment StartX=-24 StartY=19 StartZ=0 EndX=-30 EndY=19 EndZ=0
    g3: LineSegment StartX=-30 StartY=19 StartZ=0 EndX=-30 EndY=14 EndZ=0
    g4: LineSegment [constr] StartX=-24 StartY=14 StartZ=0 EndX=-24 EndY=6 EndZ=0
    g5: LineSegment [constr] StartX=-30 StartY=6 StartZ=0 EndX=-30 EndY=14 EndZ=0
  constraints (16):
    c: Coincident(g0,g1)
    c: Coincident(g1,g2)
    c: Coincident(g2,g3)
    c: Coincident(g3,g0)
    c: Horizontal(g0)
    c: Horizontal(g2)
    c: Vertical(g1)
    c: Vertical(g3)
    c: Coincident(g4,g-3)
    c: Vertical(g4)
    c: Coincident(g5,g-3)
    c: Coincident(g5,g0)
    c: Vertical(g5)
    c: Coincident(g0,g4)
    c: DistanceY(g5,g5) = 8
    c: DistanceY(g3,g3) = 5
FEATURE [Sketcher::SketchObject] Sketch075
  ArcFitTolerance = 1e-06
  FullyConstrained = true
  MakeInternals = false
  MapMode = 5
  Placement = pos=(30,0,0) rot=(0.57735,0.57735,0.57735;2.0944rad)
  sketch-geometry (6):
    g0: LineSegment StartX=-6 StartY=-10 StartZ=0 EndX=-6 EndY=-18 EndZ=0
    g1: LineSegment StartX=-6 StartY=-18 StartZ=0 EndX=-54 EndY=-18 EndZ=0
    g2: LineSegment StartX=-54 StartY=-18 StartZ=0 EndX=-54 EndY=-14 EndZ=0
    g3: LineSegment StartX=-54 StartY=-14 StartZ=0 EndX=-11 EndY=-14 EndZ=0
    g4: LineSegment StartX=-11 StartY=-14 StartZ=0 EndX=-11 EndY=-10 EndZ=0
    g5: LineSegment StartX=-11 StartY=-10 StartZ=0 EndX=-6 EndY=-10 EndZ=0
  constraints (17):
    c: Vertical(g0)
    c: Coincident(g0,g1)
    c: Horizontal(g1)
    c: Coincident(g1,g2)
    c: Vertical(g2)
    c: Coincident(g2,g3)
    c: Horizontal(g3)
    c: Coincident(g3,g4)
    c: Vertical(g4)
    c: Coincident(g4,g5)
    c: Coincident(g5,g0)
    c: DistanceY(g2,g2) = 4
    c: DistanceY(g-3,g0) = 4
    c: DistanceX(g5,g5) = 5
    c: DistanceX(g1,g1) = 48
    c: Horizontal(g5)
    c: Coincident(g0,g-4)
FEATURE [PartDesign::SubShapeBinder] Binder015  label="MountPlateHolesBinder"
  BindCopyOnChange = 0
  BindMode = 0
  ClaimChildren = false
  Context = -> Part014 [Body015.Binder015.]
  Fuse = false
  MakeFace = true
  OffsetFill = false
  OffsetIntersection = false
  OffsetJoinType = 0
  OffsetOpenResult = false
  PartialLoad = false
  Refine = true
  Relative = true
  Support = -> [Sketch045]
  _Version = 2
FEATURE [Sketcher::SketchObject] Sketch033  label="BaseScrewsSk"
  ArcFitTolerance = 1e-06
  AttachmentSupport = -> [Pad008]
  ExternalGeometry = -> [Binder015]
  FullyConstrained = true
  MakeInternals = false
  MapMode = 5
  Placement = pos=(0,0,3.6) rot=(0,0,1;0rad)
  sketch-geometry (4):
    g0: Circle CenterX=-8 CenterY=-15 CenterZ=0 NormalX=0 NormalY=0 NormalZ=1 AngleXU=0 Radius=1.7
    g1: Circle CenterX=8 CenterY=-15 CenterZ=0 NormalX=0 NormalY=0 NormalZ=1 AngleXU=0 Radius=1.7
    g2: Circle CenterX=-8 CenterY=-45 CenterZ=0 NormalX=0 NormalY=0 NormalZ=1 AngleXU=0 Radius=1.7
    g3: Circle CenterX=8 CenterY=-45 CenterZ=0 NormalX=0 NormalY=0 NormalZ=1 AngleXU=0 Radius=1.7
  constraints (8):
    c: Diameter(g0) = 3.4
    c: Coincident(g0,g-3)
    c: Coincident(g1,g-4)
    c: Coincident(g2,g-5)
    c: Coincident(g3,g-6)
    c: Equal(g0,g1)
    c: Equal(g2,g0)
    c: Equal(g3,g1)
FEATURE [PartDesign::Hole] Hole004  label="BaseScrewHoles"
  BaseFeature = -> Pocket020
  CustomThreadClearance = 0
  Depth = 25
  DepthType = 0
  Diameter = 3.2
  DrillForDepth = false
  DrillPoint = 1
  DrillPointAngle = 118
  HoleCutCountersinkAngle = 90
  HoleCutCustomValues = false
  HoleCutDepth = 0
  HoleCutDiameter = 5.2
  HoleCutType = 0
  ModelThread = false
  Profile = -> Sketch033
  Refine = true
  Suppressed = false
  Tapered = false
  TaperedAngle = 90
  ThreadClass = 0
  ThreadDepth = 25
  ThreadDepthType = 0
  ThreadDirection = 0
  ThreadFit = 1
  ThreadSize = 9
  ThreadType = 1
  Threaded = false
  UseCustomThreadClearance = false
FEATURE [PartDesign::Fillet] Fillet010  label="EdgeFillets"
  Base = -> Hole004 [Edge49,Edge46,Edge35,Edge31]
  BaseFeature = -> Hole004
  Radius = 0.5
  Refine = true
  SupportTransform = false
  Suppressed = false
  UseAllEdges = false
FEATURE [Sketcher::SketchObject] Sketch076  label="HeatBreakCooling Sk"
  ArcFitTolerance = 1e-06
  FullyConstrained = true
  MakeInternals = false
  Placement = pos=(0,0,0) rot=(0.57735,0.57735,0.57735;2.0944rad)
  expr: Constraints[9] = <<Properties>>.M3Inset
  sketch-geometry (10):
    g0: Circle CenterX=-14 CenterY=-18.5 CenterZ=0 NormalX=0 NormalY=0 NormalZ=1 AngleXU=0 Radius=2.75
    g1: Circle CenterX=-14 CenterY=-50.5 CenterZ=0 NormalX=0 NormalY=0 NormalZ=1 AngleXU=0 Radius=2.75
    g2: Circle CenterX=-46 CenterY=-18.5 CenterZ=0 NormalX=0 NormalY=0 NormalZ=1 AngleXU=0 Radius=2.75
    g3: LineSegment [constr] StartX=-14 StartY=-18.5 StartZ=0 EndX=-14 EndY=-50.5 EndZ=0
    g4: LineSegment [constr] StartX=-14 StartY=-18.5 StartZ=0 EndX=-46 EndY=-18.5 EndZ=0
    g5: Circle CenterX=-46 CenterY=-50.5 CenterZ=0 NormalX=0 NormalY=0 NormalZ=1 AngleXU=0 Radius=2.75
    g6: LineSegment [constr] StartX=-14 StartY=-50.5 StartZ=0 EndX=-46 EndY=-50.5 EndZ=0
    g7: LineSegment [constr] StartX=-46 StartY=-50.5 StartZ=0 EndX=-46 EndY=-18.5 EndZ=0
    g8: Circle CenterX=-30 CenterY=-34.5 CenterZ=0 NormalX=0 NormalY=0 NormalZ=1 AngleXU=0 Radius=19
    g9: LineSegment [constr] StartX=-46 StartY=-34.5 StartZ=0 EndX=-14 EndY=-34.5 EndZ=0
  constraints (24):
    c: Coincident(g3,g0)
    c: Coincident(g3,g1)
    c: Vertical(g3)
    c: Coincident(g4,g0)
    c: Coincident(g4,g2)
    c: Horizontal(g4)
    c: DistanceY(g3,g3) = 32
    c: DistanceX(g0,g-1) = 14
    c: DistanceX(g4,g4) = 32
    c: Diameter(g2) = 5.5
    c: Equal(g2,g0)
    c: Equal(g0,g1)
    c: DistanceY(g0,g-1) = 18.5
    c: Coincident(g6,g1)
    c: Coincident(g6,g5)
    c: Horizontal(g6)
    c: Coincident(g7,g5)
    c: Coincident(g7,g2)
    c: Vertical(g7)
    c: Equal(g5,g2)
    c: Symmetric(g7,g7,g9)
    c: Symmetric(g3,g3,g9)
    c: Diameter(g8) = 38
    c: Symmetric(g9,g9,g8)
FEATURE [PartDesign::SubShapeBinder] Binder016  label="CoolingMountBinder"
  BindCopyOnChange = 0
  BindMode = 0
  ClaimChildren = false
  Context = -> Part019 [Body032.Binder016.]
  Fuse = false
  MakeFace = true
  OffsetFill = false
  OffsetIntersection = false
  OffsetJoinType = 0
  OffsetOpenResult = false
  PartialLoad = false
  Refine = true
  Relative = true
  Support = -> [Sketch076]
  _Version = 2
FEATURE [PartDesign::Plane] DatumPlane002
  AttachmentOffset = pos=(0,0,-24) rot=(0,0,1;0rad)
  AttachmentSupport = -> [YZ_Plane052]
  Length = 90.4434
  MapMode = 5
  Placement = pos=(-24,0,0) rot=(0.57735,0.57735,0.57735;2.0944rad)
  ResizeMode = 0
  Width = 94.9434
FEATURE [Sketcher::SketchObject] Sketch077
  ArcFitTolerance = 1e-06
  AttachmentSupport = -> [DatumPlane002]
  ExternalGeometry = -> [Binder016]
  FullyConstrained = true
  MakeInternals = false
  MapMode = 5
  Placement = pos=(-24,0,0) rot=(0.57735,0.57735,0.57735;2.0944rad)
  sketch-geometry (10):
    g0: LineSegment StartX=-50 StartY=-14.5 StartZ=0 EndX=-50 EndY=-54.5 EndZ=0
    g1: LineSegment StartX=-50 StartY=-54.5 StartZ=0 EndX=-10 EndY=-54.5 EndZ=0
    g2: LineSegment StartX=-10 StartY=-54.5 StartZ=0 EndX=-10 EndY=-14.5 EndZ=0
    g3: LineSegment StartX=-10 StartY=-14.5 StartZ=0 EndX=-50 EndY=-14.5 EndZ=0
    g4: LineSegment [constr] StartX=-50 StartY=-14.5 StartZ=0 EndX=-10 EndY=-54.5 EndZ=0
    g5: Circle CenterX=-30 CenterY=-34.5 CenterZ=0 NormalX=0 NormalY=0 NormalZ=1 AngleXU=0 Radius=18
    g6: Circle CenterX=-46 CenterY=-18.5 CenterZ=0 NormalX=0 NormalY=0 NormalZ=1 AngleXU=0 Radius=1.7
    g7: Circle CenterX=-14 CenterY=-18.5 CenterZ=0 NormalX=0 NormalY=0 NormalZ=1 AngleXU=0 Radius=1.7
    g8: Circle CenterX=-14 CenterY=-50.5 CenterZ=0 NormalX=0 NormalY=0 NormalZ=1 AngleXU=0 Radius=1.7
    g9: Circle CenterX=-46 CenterY=-50.5 CenterZ=0 NormalX=0 NormalY=0 NormalZ=1 AngleXU=0 Radius=1.7
  constraints (23):
    c: Coincident(g0,g1)
    c: Coincident(g1,g2)
    c: Coincident(g2,g3)
    c: Coincident(g3,g0)
    c: Vertical(g0)
    c: Vertical(g2)
    c: Horizontal(g1)
    c: Horizontal(g3)
    c: Coincident(g4,g0)
    c: Coincident(g4,g1)
    c: Symmetric(g0,g1,g-3)
    c: DistanceY(g0,g0) = 40
    c: Equal(g0,g3)
    c: Coincident(g5,g-3)
    c: Distance(g-3,g5) = 1
    c: Coincident(g6,g-5)
    c: Coincident(g7,g-4)
    c: Coincident(g8,g-7)
    c: Coincident(g9,g-6)
    c: Diameter(g6) = 3.4
    c: Equal(g6,g7)
    c: Equal(g6,g9)
    c: Equal(g7,g8)
FEATURE [PartDesign::Pad] Pad030  label="DuctFlange"
  Direction = (1,0,0)
  Length = 1.5
  Length2 = 10
  Placement = pos=(-24,0,0) rot=(0.57735,0.57735,0.57735;2.0944rad)
  Profile = -> Sketch077
  ReferenceAxis = -> Sketch077 [N_Axis]
  Refine = true
  Reversed = true
  Suppressed = false
  Type = 0
FEATURE [Sketcher::SketchObject] Sketch078  label="LoftSk001"
  ArcFitTolerance = 1e-06
  AttachmentSupport = -> [Pad030]
  ExternalGeometry = -> [Pad030]
  FullyConstrained = true
  MakeInternals = false
  MapMode = 5
  Placement = pos=(-24,0,0) rot=(0.57735,0.57735,0.57735;2.0944rad)
  sketch-geometry (13):
    g0: ArcOfCircle CenterX=-30 CenterY=-34.5 CenterZ=0 NormalX=0 NormalY=0 NormalZ=1 AngleXU=0 Radius=18 StartAngle=1.57635 EndAngle=4.70683
    g1: LineSegment StartX=-30.1 StartY=-16.5003 StartZ=0 EndX=-29.9 EndY=-16.5003 EndZ=0
    g2: LineSegment StartX=-30.1 StartY=-52.4997 StartZ=0 EndX=-29.9 EndY=-52.4997 EndZ=0
    g3: ArcOfCircle CenterX=-30 CenterY=-34.5 CenterZ=0 NormalX=0 NormalY=0 NormalZ=1 AngleXU=0 Radius=18 StartAngle=4.71794 EndAngle=7.84843
    g4: ArcOfCircle CenterX=-30 CenterY=-34.5 CenterZ=0 NormalX=0 NormalY=0 NormalZ=1 AngleXU=0 Radius=19 StartAngle=4.71765 EndAngle=7.84872
    g5: LineSegment StartX=-30.1 StartY=-15.5003 StartZ=0 EndX=-29.9 EndY=-15.5003 EndZ=0
    g6: LineSegment StartX=-30.1 StartY=-53.4997 StartZ=0 EndX=-29.9 EndY=-53.4997 EndZ=0
    g7: ArcOfCircle CenterX=-30 CenterY=-34.5 CenterZ=0 NormalX=0 NormalY=0 NormalZ=1 AngleXU=0 Radius=19 StartAngle=1.57606 EndAngle=4.70713
    g8: LineSegment [constr] StartX=-30.1 StartY=-15.5003 StartZ=0 EndX=-30.1 EndY=-16.5003 EndZ=0
    g9: LineSegment [constr] StartX=-29.9 StartY=-15.5003 StartZ=0 EndX=-29.9 EndY=-16.5003 EndZ=0
    g10: LineSegment [constr] StartX=-30.1 StartY=-16.5003 StartZ=0 EndX=-30.1 EndY=-52.4997 EndZ=0
    g11: LineSegment [constr] StartX=-29.9 StartY=-16.5003 StartZ=0 EndX=-29.9 EndY=-52.4997 EndZ=0
    g12: LineSegment [constr] StartX=-30.1 StartY=-52.4997 StartZ=0 EndX=-30.1 EndY=-53.4997 EndZ=0
  constraints (36):
    c: Coincident(g0,g-3)
    c: Equal(g0,g-3)
    c: Horizontal(g1)
    c: PointOnObject(g2,g3)
    c: Horizontal(g2)
    c: Coincident(g3,g1)
    c: Coincident(g0,g1)
    c: Equal(g0,g3)
    c: Coincident(g0,g2)
    c: PointOnObject(g3,g2)
    c: Coincident(g0,g3)
    c: Coincident(g4,g0)
    c: PointOnObject(g5,g7)
    c: Horizontal(g5)
    c: Horizontal(g6)
    c: Coincident(g7,g6)
    c: Coincident(g4,g6)
    c: Equal(g4,g7)
    c: Coincident(g4,g5)
    c: PointOnObject(g7,g5)
    c: Coincident(g4,g7)
    c: Coincident(g8,g5)
    c: Coincident(g8,g0)
    c: Vertical(g8)
    c: Coincident(g9,g4)
    c: Coincident(g9,g1)
    c: Coincident(g10,g0)
    c: Coincident(g10,g0)
    c: Vertical(g10)
    c: Coincident(g11,g1)
    c: Coincident(g11,g2)
    c: Coincident(g12,g0)
    c: Coincident(g12,g6)
    c: Vertical(g12)
    c: Distance(g3,g4) = 1
    c: DistanceX(g7,g4) = 0.2
FEATURE [Sketcher::SketchObject] Sketch079  label="LoftSk002"
  ArcFitTolerance = 1e-06
  AttachmentOffset = pos=(0,0,15) rot=(0,0,1;0rad)
  AttachmentSupport = -> [Pad030]
  ExternalGeometry = -> [Pad030]
  FullyConstrained = true
  MakeInternals = false
  MapMode = 5
  Placement = pos=(-9,0,0) rot=(0.57735,0.57735,0.57735;2.0944rad)
  sketch-geometry (27):
    g0: ArcOfCircle CenterX=-30 CenterY=-33.5 CenterZ=0 NormalX=0 NormalY=0 NormalZ=1 AngleXU=0 Radius=12.8062 StartAngle=2.46685 EndAngle=2.65398
    g1: ArcOfCircle CenterX=-30 CenterY=-33.5 CenterZ=0 NormalX=0 NormalY=0 NormalZ=1 AngleXU=0 Radius=13.4536 StartAngle=5.55037 EndAngle=5.82092
    g2: LineSegment StartX=-40 StartY=-25.5 StartZ=0 EndX=-20 EndY=-25.5 EndZ=0
    g3: LineSegment StartX=-40 StartY=-41.5 StartZ=0 EndX=-20 EndY=-41.5 EndZ=0
    g4: ArcOfCircle CenterX=-30 CenterY=-33.5 CenterZ=0 NormalX=0 NormalY=0 NormalZ=1 AngleXU=0 Radius=12.8062 StartAngle=5.60844 EndAngle=5.79557
    g5: LineSegment StartX=-40 StartY=-24.5 StartZ=0 EndX=-20 EndY=-24.5 EndZ=0
    g6: LineSegment StartX=-40 StartY=-42.5 StartZ=0 EndX=-20 EndY=-42.5 EndZ=0
    g7: ArcOfCircle CenterX=-30 CenterY=-33.5 CenterZ=0 NormalX=0 NormalY=0 NormalZ=1 AngleXU=0 Radius=13.4536 StartAngle=2.40878 EndAngle=2.67933
    g8: LineSegment [constr] StartX=-40 StartY=-24.5 StartZ=0 EndX=-40 EndY=-25.5 EndZ=0
    g9: LineSegment [constr] StartX=-20 StartY=-24.5 StartZ=0 EndX=-20 EndY=-25.5 EndZ=0
    g10: LineSegment [constr] StartX=-40 StartY=-41.5 StartZ=0 EndX=-40 EndY=-42.5 EndZ=0
    g11: LineSegment [constr] StartX=-20 StartY=-41.5 StartZ=0 EndX=-20 EndY=-42.5 EndZ=0
    g12: LineSegment [constr] StartX=-40 StartY=-25.5 StartZ=0 EndX=-40 EndY=-41.5 EndZ=0
    g13: LineSegment [constr] StartX=-20 StartY=-25.5 StartZ=0 EndX=-20 EndY=-41.5 EndZ=0
    g14: LineSegment StartX=-41.3137 StartY=-27.5 StartZ=0 EndX=-41.3137 EndY=-39.5 EndZ=0
    g15: LineSegment StartX=-18.6863 StartY=-27.5 StartZ=0 EndX=-18.6863 EndY=-39.5 EndZ=0
    g16: LineSegment [constr] StartX=-41.3137 StartY=-27.5 StartZ=0 EndX=-18.6863 EndY=-27.5 EndZ=0
    g17: LineSegment [constr] StartX=-41.3137 StartY=-39.5 StartZ=0 EndX=-18.6863 EndY=-39.5 EndZ=0
    g18: ArcOfCircle CenterX=-30 CenterY=-33.5 CenterZ=0 NormalX=0 NormalY=0 NormalZ=1 AngleXU=0 Radius=12.8062 StartAngle=3.62921 EndAngle=3.81633
    g19: ArcOfCircle CenterX=-30 CenterY=-33.5 CenterZ=0 NormalX=0 NormalY=0 NormalZ=1 AngleXU=0 Radius=12.8062 StartAngle=0.487616 EndAngle=0.674741
    g20: LineSegment StartX=-42.0416 StartY=-27.5 StartZ=0 EndX=-42.0416 EndY=-39.5 EndZ=0
    g21: LineSegment StartX=-17.9584 StartY=-27.5 StartZ=0 EndX=-17.9584 EndY=-39.5 EndZ=0
    g22: ArcOfCircle CenterX=-30 CenterY=-33.5 CenterZ=0 NormalX=0 NormalY=0 NormalZ=1 AngleXU=0 Radius=13.4536 StartAngle=3.60386 EndAngle=3.87441
    g23: ArcOfCircle CenterX=-30 CenterY=-33.5 CenterZ=0 NormalX=0 NormalY=0 NormalZ=1 AngleXU=0 Radius=13.4536 StartAngle=0.462265 EndAngle=0.732815
    g24: LineSegment [constr] StartX=-18.6863 StartY=-27.5 StartZ=0 EndX=-17.9584 EndY=-27.5 EndZ=0
    g25: LineSegment [constr] StartX=-42.0416 StartY=-27.5 StartZ=0 EndX=-41.3137 EndY=-27.5 EndZ=0
    g26: LineSegment [constr] StartX=-30 StartY=-33.5 StartZ=0 EndX=-30 EndY=-34.5 EndZ=0
  constraints (78):
    c: Coincident(g1,g0)
    c: Horizontal(g2)
    c: PointOnObject(g3,g4)
    c: Horizontal(g3)
    c: Coincident(g19,g2)
    c: Coincident(g0,g2)
    c: Equal(g0,g4)
    c: Coincident(g18,g3)
    c: PointOnObject(g4,g3)
    c: Coincident(g0,g4)
    c: PointOnObject(g5,g7)
    c: Horizontal(g5)
    c: Horizontal(g6)
    c: Coincident(g22,g6)
    c: Coincident(g1,g6)
    c: Equal(g1,g7)
    c: Coincident(g23,g5)
    c: PointOnObject(g7,g5)
    c: Coincident(g1,g7)
    c: Coincident(g8,g5)
    c: Coincident(g8,g0)
    c: Vertical(g8)
    c: Coincident(g9,g23)
    c: Coincident(g9,g2)
    c: Coincident(g10,g18)
    c: Coincident(g10,g6)
    c: Vertical(g10)
    c: Coincident(g11,g3)
    c: Coincident(g11,g1)
    c: Coincident(g12,g0)
    c: Coincident(g12,g18)
    c: Vertical(g12)
    c: Coincident(g13,g2)
    c: Coincident(g13,g4)
    c: DistanceY(g12,g12) = 16
    c: DistanceX(g5,g5) = 20
    c: PointOnObject(g14,g18)
    c: Vertical(g14)
    c: PointOnObject(g15,g19)
    c: PointOnObject(g15,g4)
    c: Vertical(g15)
    c: Coincident(g16,g14)
    c: Coincident(g16,g15)
    c: Horizontal(g16)
    c: Coincident(g17,g14)
    c: Coincident(g17,g15)
    c: Equal(g0,g18)
    c: Coincident(g0,g14)
    c: PointOnObject(g18,g17)
    c: Coincident(g0,g18)
    c: Equal(g4,g19)
    c: PointOnObject(g4,g17)
    c: PointOnObject(g19,g15)
    c: Coincident(g4,g19)
    c: PointOnObject(g20,g22)
    c: Vertical(g20)
    c: PointOnObject(g21,g23)
    c: Vertical(g21)
    c: Equal(g7,g22)
    c: Coincident(g7,g20)
    c: PointOnObject(g22,g20)
    c: Coincident(g7,g22)
    c: Equal(g1,g23)
    c: Coincident(g1,g21)
    c: PointOnObject(g23,g21)
    c: Coincident(g1,g23)
    c: DistanceY(g9,g9) = 1
    c: Coincident(g24,g19)
    c: Coincident(g24,g21)
    c: Horizontal(g24)
    c: Coincident(g25,g7)
    c: Coincident(g25,g0)
    c: Horizontal(g25)
    c: DistanceY(g20,g20) = 12
    c: Coincident(g26,g0)
    c: Coincident(g26,g-3)
    c: Vertical(g26)
    c: DistanceY(g26,g0) = 1
FEATURE [PartDesign::AdditiveLoft] AdditiveLoft
  BaseFeature = -> Pad030
  Closed = false
  Placement = pos=(-24,0,0) rot=(0.57735,0.57735,0.57735;2.0944rad)
  Profile = -> Sketch078
  Refine = true
  Ruled = false
  Sections = -> [Sketch079]
  Suppressed = false
FEATURE [PartDesign::SubShapeBinder] Binder017  label="FilamentPathBinder001"
  BindCopyOnChange = 0
  BindMode = 0
  ClaimChildren = false
  Context = -> Part019 [Body032.Binder017.]
  Fuse = false
  MakeFace = true
  OffsetFill = false
  OffsetIntersection = false
  OffsetJoinType = 0
  OffsetOpenResult = false
  PartialLoad = false
  Refine = true
  Relative = true
  Support = -> [Sketch006]
  _Version = 2
FEATURE [Sketcher::SketchObject] Sketch080
  ArcFitTolerance = 1e-06
  AttachmentSupport = -> [AdditiveLoft]
  ExternalGeometry = -> [Binder017]
  FullyConstrained = true
  MakeInternals = false
  MapMode = 5
  Placement = pos=(-24,-1.6e-15,-14.5) rot=(0,0,-1;1.5708rad)
  sketch-geometry (1):
    g0: Circle CenterX=30 CenterY=24 CenterZ=0 NormalX=0 NormalY=0 NormalZ=1 AngleXU=0 Radius=12.5
  constraints (2):
    c: Coincident(g0,g-3)
    c: Diameter(g0) = 25
FEATURE [PartDesign::Pocket] Pocket038  label="HotendCutoutPk"
  BaseFeature = -> AdditiveLoft
  Direction = (0,0,-1)
  Length = 37
  Length2 = 5
  Placement = pos=(-24,0,0) rot=(0.57735,0.57735,0.57735;2.0944rad)
  Profile = -> Sketch080
  ReferenceAxis = -> Sketch080 [N_Axis]
  Refine = true
  Suppressed = false
  Type = 0
FEATURE [PartDesign::Fillet] Fillet011  label="CornersFillet"
  Base = -> Pocket038 [Edge5,Edge1,Edge8,Edge2]
  BaseFeature = -> Pocket038
  Placement = pos=(-24,0,0) rot=(0.57735,0.57735,0.57735;2.0944rad)
  Radius = 2
  Refine = true
  SupportTransform = false
  Suppressed = false
  UseAllEdges = false
FEATURE [PartDesign::Chamfer] Chamfer011  label="FanInletCh"
  Angle = 45
  Base = -> Fillet011 [Edge37]
  BaseFeature = -> Fillet011
  ChamferType = 0
  FlipDirection = false
  Placement = pos=(-24,0,0) rot=(0.57735,0.57735,0.57735;2.0944rad)
  Refine = true
  Size = 1.4
  Size2 = 1.49
  SupportTransform = false
  Suppressed = false
  UseAllEdges = false
FEATURE [PartDesign::Body] Body032  label="HeatBreakDuctBody"
  AllowCompound = false
  Group = -> [Binder016,Binder017,DatumPlane002,Sketch077,Pad030,Sketch078,Sketch079,AdditiveLoft,Sketch080,Pocket038,Fillet011,Chamfer011]
  Origin = -> Origin052
  Tip = -> Chamfer011
FEATURE [App::Part] Part019  label="HeatBreakFanDuct"
  Group = -> [Body032]
  Origin = -> Origin051
FEATURE [PartDesign::SubShapeBinder] Binder018  label="ToolBottomBaseBinder001"
  BindCopyOnChange = 0
  BindMode = 0
  ClaimChildren = false
  Context = -> Part020 [Body033.Binder018.]
  Fuse = false
  MakeFace = true
  OffsetFill = false
  OffsetIntersection = false
  OffsetJoinType = 0
  OffsetOpenResult = false
  PartialLoad = false
  Refine = true
  Relative = true
  Support = -> [Sketch043]
  _Version = 2
FEATURE [PartDesign::Plane] DatumPlane003
  AttachmentSupport = -> [Binder018]
  Length = 69.0604
  MapMode = 5
  Placement = pos=(0,0,-55) rot=(0,0,1;0rad)
  ResizeMode = 0
  Width = 111.81
FEATURE [Sketcher::SketchObject] Sketch081  label="SketchVortex"
  ArcFitTolerance = 1e-06
  AttachmentSupport = -> [DatumPlane003]
  FullyConstrained = false
  MakeInternals = false
  MapMode = 5
  Placement = pos=(0,0,-55) rot=(0,1,0;3.14159rad)
  sketch-geometry (31):
    g0: Circle CenterX=0 CenterY=10.056 CenterZ=0 NormalX=0 NormalY=0 NormalZ=1 AngleXU=0 Radius=4.30512
    g1: LineSegment StartX=7.24325 StartY=-70.2697 StartZ=0 EndX=-6.76176 EndY=-70.2697 EndZ=0
    g2: LineSegment StartX=-6.76176 StartY=-70.2697 StartZ=0 EndX=-29.0908 EndY=-70.2697 EndZ=0
    g3: LineSegment StartX=-29.0908 StartY=-70.2697 StartZ=0 EndX=-29.0908 EndY=-1.65702 EndZ=0
    g4: LineSegment StartX=-29.0908 StartY=-1.65702 StartZ=0 EndX=25.0039 EndY=-1.65702 EndZ=0
    g5: LineSegment StartX=25.0039 StartY=-1.65702 StartZ=0 EndX=25.0039 EndY=-36.7545 EndZ=0
    g6: LineSegment StartX=8.09836 StartY=-59.8946 StartZ=0 EndX=-12.6479 EndY=-59.8946 EndZ=0
    g7: LineSegment StartX=-12.6479 StartY=-59.8946 StartZ=0 EndX=-12.6479 EndY=-30.4731 EndZ=0
    g8: LineSegment StartX=-12.6479 StartY=-30.4731 StartZ=0 EndX=-8.03987 EndY=-30.5148 EndZ=0
    g9: LineSegment StartX=7.97564 StartY=-63.0646 StartZ=0 EndX=-16.5189 EndY=-63.0646 EndZ=0
    g10: LineSegment StartX=-16.5189 StartY=-63.0646 StartZ=0 EndX=-16.5189 EndY=-26.2125 EndZ=0
    g11: LineSegment StartX=-16.5189 StartY=-26.2125 StartZ=0 EndX=-12.9176 EndY=-22.1763 EndZ=0
    g12: LineSegment StartX=-22.9375 StartY=-43.8654 StartZ=0 EndX=-22.9375 EndY=-10.0434 EndZ=0
    g13: LineSegment StartX=-22.9375 StartY=-10.0434 StartZ=0 EndX=4.03325 EndY=-9.91259 EndZ=0
    g14: LineSegment StartX=4.03325 StartY=-9.91259 StartZ=0 EndX=7.43292 EndY=-13.0761 EndZ=0
    g15: LineSegment StartX=12.4559 StartY=-29.9758 StartZ=0 EndX=15.6086 EndY=-26.3307 EndZ=0
    g16: LineSegment StartX=15.6086 StartY=-26.3307 StartZ=0 EndX=14.8999 EndY=-9.44013 EndZ=0
    g17: LineSegment StartX=21.0531 StartY=-32.9488 StartZ=0 EndX=22.9351 EndY=-19.8104 EndZ=0
    g18: LineSegment StartX=0.135438 StartY=-19.5981 StartZ=0 EndX=0.135438 EndY=-16.0546 EndZ=0
    g19: LineSegment StartX=-12.9176 StartY=-22.1763 StartZ=0 EndX=-7.60117 EndY=-21.9506 EndZ=0
    g20: LineSegment StartX=7.43292 StartY=-13.0761 StartZ=0 EndX=7.47276 EndY=-19.8932 EndZ=0
    g21: LineSegment StartX=21.0531 StartY=-32.9488 StartZ=0 EndX=18.589 EndY=-37.4786 EndZ=0
    g22: LineSegment StartX=18.589 StartY=-37.4786 StartZ=0 EndX=9.0987 EndY=-37.4786 EndZ=0
    g23: LineSegment StartX=12.4559 StartY=-29.9758 StartZ=0 EndX=9.03775 EndY=-30.1104 EndZ=0
    g24: LineSegment StartX=7.83192 StartY=-56.2028 StartZ=0 EndX=-0.236073 EndY=-56.2028 EndZ=0
    g25: LineSegment StartX=-0.236073 StartY=-56.2028 StartZ=0 EndX=-0.236073 EndY=-45.0649 EndZ=0
    g26: LineSegment StartX=8.09836 StartY=-59.8946 StartZ=0 EndX=8.06262 EndY=-59.2808 EndZ=0
    g27: LineSegment StartX=8.06262 StartY=-59.2808 StartZ=0 EndX=-4.03797 EndY=-59.2808 EndZ=0
    g28: LineSegment StartX=-4.03797 StartY=-59.2808 StartZ=0 EndX=-4.03797 EndY=-45.1103 EndZ=0
    g29: LineSegment StartX=-4.03797 StartY=-45.1103 StartZ=0 EndX=-8.03987 EndY=-45.1103 EndZ=0
    g30: LineSegment StartX=-8.03987 StartY=-45.1103 StartZ=0 EndX=-8.03987 EndY=-30.5148 EndZ=0
  constraints (41):
    c: PointOnObject(g0,g-2)
    c: Horizontal(g1)
    c: Coincident(g1,g2)
    c: Horizontal(g2)
    c: Coincident(g2,g3)
    c: Vertical(g3)
    c: Coincident(g3,g4)
    c: Horizontal(g4)
    c: Coincident(g4,g5)
    c: Vertical(g5)
    c: Horizontal(g6)
    c: Coincident(g6,g7)
    c: Vertical(g7)
    c: Coincident(g7,g8)
    c: Horizontal(g9)
    c: Coincident(g9,g10)
    c: Vertical(g10)
    c: Vertical(g12)
    c: Coincident(g12,g13)
    c: Coincident(g13,g14)
    c: Coincident(g15,g16)
    c: Coincident(g19,g11)
    c: Coincident(g20,g14)
    c: Coincident(g21,g17)
    c: Coincident(g22,g21)
    c: Horizontal(g22)
    c: Coincident(g23,g15)
    c: Horizontal(g24)
    c: Coincident(g25,g24)
    c: Vertical(g25)
    c: Coincident(g11,g10)
    c: Coincident(g6,g26)
    c: Coincident(g26,g27)
    c: Horizontal(g27)
    c: Coincident(g27,g28)
    c: Vertical(g28)
    c: Coincident(g28,g29)
    c: Horizontal(g29)
    c: Coincident(g29,g30)
    c: Coincident(g30,g8)
    c: Vertical(g30)
FEATURE [PartDesign::SubShapeBinder] Binder019  label="CoolingDuctBaseBinder001"
  BindCopyOnChange = 0
  BindMode = 0
  ClaimChildren = false
  Context = -> Part020 [Body033.Binder019.]
  Fuse = false
  MakeFace = true
  OffsetFill = false
  OffsetIntersection = false
  OffsetJoinType = 0
  OffsetOpenResult = false
  PartialLoad = false
  Refine = true
  Relative = true
  Support = -> [Sketch042]
  _Version = 2
FEATURE [Sketcher::SketchObject] Sketch082
  ArcFitTolerance = 1e-06
  AttachmentSupport = -> [DatumPlane003]
  FullyConstrained = false
  MakeInternals = false
  MapMode = 5
  Placement = pos=(0,0,-55) rot=(0,1,0;3.14159rad)
  sketch-geometry (19):
    g0: LineSegment StartX=7.96311 StartY=-71.1114 StartZ=0 EndX=-28.7892 EndY=-71.1114 EndZ=0
    g1: LineSegment StartX=-18.7892 StartY=-38.4173 StartZ=0 EndX=-18.7892 EndY=-55.925 EndZ=0
    g2: LineSegment StartX=-18.7892 StartY=-55.925 StartZ=0 EndX=7.96311 EndY=-55.925 EndZ=0
    g3: LineSegment StartX=18.7892 StartY=-55.925 StartZ=0 EndX=18.7892 EndY=-38.4173 EndZ=0
    g4: LineSegment StartX=18.7892 StartY=-38.4173 StartZ=0 EndX=12.7582 EndY=-37.3789 EndZ=0
    g5: LineSegment StartX=28.7892 StartY=-71.1114 StartZ=0 EndX=28.7892 EndY=-29.992 EndZ=0
    g6: LineSegment StartX=28.7892 StartY=-29.992 StartZ=0 EndX=14.455 EndY=-27.5239 EndZ=0
    g7: LineSegment StartX=-28.7892 StartY=-29.992 StartZ=0 EndX=-14.455 EndY=-27.5239 EndZ=0
    g8: LineSegment StartX=-18.7892 StartY=-38.4173 StartZ=0 EndX=-12.7582 EndY=-37.3789 EndZ=0
    g9: LineSegment [constr] StartX=-14.455 StartY=-27.5239 StartZ=0 EndX=14.455 EndY=-27.5239 EndZ=0
    g10: LineSegment [constr] StartX=-12.7582 StartY=-37.3789 StartZ=0 EndX=12.7582 EndY=-37.3789 EndZ=0
    g11: LineSegment [constr] StartX=7.96311 StartY=-55.925 StartZ=0 EndX=7.96311 EndY=-71.1114 EndZ=0
    g12: LineSegment StartX=7.96311 StartY=-71.1114 StartZ=0 EndX=28.7892 EndY=-71.1114 EndZ=0
    g13: LineSegment StartX=-14.455 StartY=-27.5239 StartZ=0 EndX=-12.7582 EndY=-37.3789 EndZ=0
    g14: LineSegment StartX=-28.7892 StartY=-29.992 StartZ=0 EndX=-28.7892 EndY=-55.925 EndZ=0
    g15: LineSegment StartX=-28.7892 StartY=-55.925 StartZ=0 EndX=-28.7892 EndY=-71.1114 EndZ=0
    g16: LineSegment [constr] StartX=-28.7892 StartY=-55.925 StartZ=0 EndX=-18.7892 EndY=-55.925 EndZ=0
    g17: LineSegment StartX=14.455 StartY=-27.5239 StartZ=0 EndX=12.7582 EndY=-37.3789 EndZ=0
    g18: LineSegment StartX=7.96311 StartY=-55.925 StartZ=0 EndX=18.7892 EndY=-55.925 EndZ=0
  constraints (42):
    c: Horizontal(g0)
    c: Vertical(g1)
    c: Coincident(g1,g2)
    c: Horizontal(g2)
    c: Vertical(g3)
    c: Coincident(g3,g4)
    c: Vertical(g5)
    c: Coincident(g5,g6)
    c: Coincident(g8,g1)
    c: Coincident(g9,g7)
    c: Coincident(g9,g6)
    c: Coincident(g10,g8)
    c: Coincident(g10,g4)
    c: Symmetric(g7,g6,g-2)
    c: Symmetric(g7,g5,g-2)
    c: Symmetric(g1,g3,g-2)
    c: Symmetric(g8,g4,g-2)
    c: Parallel(g8,g7)
    c: Coincident(g11,g2)
    c: Coincident(g11,g0)
    c: Vertical(g11)
    c: Coincident(g12,g0)
    c: Coincident(g12,g5)
    c: Horizontal(g12)
    c: Coincident(g13,g7)
    c: Coincident(g13,g8)
    c: Perpendicular(g13,g7)
    c: Coincident(g14,g7)
    c: Vertical(g14)
    c: Coincident(g15,g0)
    c: Vertical(g15)
    c: Coincident(g16,g14)
    c: Coincident(g16,g1)
    c: Horizontal(g16)
    c: Coincident(g15,g14)
    c: Equal(g16,g13)
    c: DistanceX(g16,g16) = 10
    c: Coincident(g17,g6)
    c: Coincident(g17,g4)
    c: Coincident(g18,g2)
    c: Coincident(g18,g3)
    c: Horizontal(g18)
FEATURE [Sketcher::SketchObject] Sketch083  label="HornsPath"
  ArcFitTolerance = 1e-06
  AttachmentSupport = -> [DatumPlane003]
  FullyConstrained = false
  MakeInternals = false
  MapMode = 5
  Placement = pos=(0,0,-55) rot=(0,0,1;0rad)
  sketch-geometry (8):
    g0: GeomPoint [constr] X=-13.3953 Y=-32.3192 Z=0
    g1: GeomPoint [constr] X=-30.3786 Y=-49.9224 Z=0
    g2: GeomPoint [constr] X=-9.7665 Y=-64.7383 Z=0
    g3: BSplineCurve PolesCount=4 KnotsCount=2 Degree=3 IsPeriodic=0
    g4-g7: Circle [constr] x4 (B-spline internal-alignment scaffolding for g3; pole/knot coordinates omitted)
  constraints (11):
    c: InternalAlignment(g0,g3)
    c: PointOnObject(g1,g3)
    c: InternalAlignment(g2,g3)
    c: InternalAlignment(g4,g3)
    c: Weight(g4) = 1
    c: InternalAlignment(g5,g3)
    c: Equal(g5,g4)
    c: InternalAlignment(g6,g3)
    c: Equal(g6,g4)
    c: InternalAlignment(g7,g3)
    c: Equal(g7,g4)
FEATURE [Sketcher::SketchObject] Sketch091
  ArcFitTolerance = 1e-06
  AttachmentOffset = pos=(0,0,-1) rot=(0,0,1;0rad)
  FullyConstrained = true
  MakeInternals = false
  MapMode = 5
  Placement = pos=(0,0,-66) rot=(1,0,0;3.14159rad)
  sketch-geometry (10):
    g0: LineSegment StartX=-28.5 StartY=71.25 StartZ=0 EndX=-28.5 EndY=55.75 EndZ=0
    g1: LineSegment StartX=-28.5 StartY=55.75 StartZ=0 EndX=-9 EndY=55.75 EndZ=0
    g2: LineSegment StartX=-9 StartY=55.75 StartZ=0 EndX=-9 EndY=53.75 EndZ=0
    g3: LineSegment StartX=-9 StartY=53.75 StartZ=0 EndX=9 EndY=53.75 EndZ=0
    g4: LineSegment StartX=9 StartY=53.75 StartZ=0 EndX=9 EndY=55.75 EndZ=0
    g5: LineSegment [constr] StartX=9 StartY=55.75 StartZ=0 EndX=9 EndY=71.25 EndZ=0
    g6: LineSegment [constr] StartX=9 StartY=71.25 StartZ=0 EndX=-6.5 EndY=71.25 EndZ=0
    g7: LineSegment StartX=-6.5 StartY=71.25 StartZ=0 EndX=-28.5 EndY=71.25 EndZ=0
    g8: ArcOfCircle CenterX=-6.5 CenterY=55.75 CenterZ=0 NormalX=0 NormalY=0 NormalZ=1 AngleXU=0 Radius=15.5 StartAngle=1e-16 EndAngle=1.5708
    g9: LineSegment [constr] StartX=-6.5 StartY=55.75 StartZ=0 EndX=-9 EndY=55.75 EndZ=0
  constraints (28):
    c: Vertical(g0)
    c: Coincident(g0,g1)
    c: Horizontal(g1)
    c: Coincident(g1,g2)
    c: Vertical(g2)
    c: Coincident(g2,g3)
    c: Horizontal(g3)
    c: Coincident(g3,g4)
    c: Vertical(g4)
    c: Coincident(g4,g5)
    c: Vertical(g5)
    c: Coincident(g6,g5)
    c: Horizontal(g6)
    c: Coincident(g7,g6)
    c: Coincident(g7,g0)
    c: Horizontal(g7)
    c: Coincident(g8,g6)
    c: PointOnObject(g2,g-5)
    c: DistanceX(g-5,g2) = 1
    c: DistanceX(g3,g-5) = 1
    c: DistanceY(g-3,g0) = 1
    c: DistanceX(g-3,g0) = 1
    c: DistanceY(g5,g-4) = 1
    c: Tangent(g7,g8)
    c: Tangent(g8,g4) = -1.5708
    c: Coincident(g9,g8)
    c: Coincident(g9,g1)
    c: Horizontal(g9)
FEATURE [Sketcher::SketchObject] Sketch095
  ArcFitTolerance = 1e-06
  AttachmentSupport = -> [DatumPlane003]
  FullyConstrained = true
  MakeInternals = false
  MapMode = 5
  Placement = pos=(0,0,-55) rot=(0,0,1;0rad)
  sketch-geometry (6):
    g0: LineSegment StartX=-29.5 StartY=-54.75 StartZ=0 EndX=-29.5 EndY=-72.25 EndZ=0
    g1: LineSegment StartX=-29.5 StartY=-72.25 StartZ=0 EndX=10 EndY=-72.25 EndZ=0
    g2: LineSegment StartX=10 StartY=-72.25 StartZ=0 EndX=10 EndY=-53.75 EndZ=0
    g3: LineSegment StartX=10 StartY=-53.75 StartZ=0 EndX=-10 EndY=-53.75 EndZ=0
    g4: LineSegment StartX=-10 StartY=-53.75 StartZ=0 EndX=-10 EndY=-54.75 EndZ=0
    g5: LineSegment StartX=-10 StartY=-54.75 StartZ=0 EndX=-29.5 EndY=-54.75 EndZ=0
  constraints (17):
    c: Vertical(g0)
    c: Coincident(g0,g1)
    c: Horizontal(g1)
    c: Coincident(g1,g2)
    c: Vertical(g2)
    c: Coincident(g2,g3)
    c: Coincident(g3,g4)
    c: Coincident(g4,g5)
    c: Coincident(g5,g0)
    c: Horizontal(g5)
    c: Vertical(g4)
    c: Symmetric(g3,g2,g-2)
    c: DistanceX(g3,g3) = 20
    c: DistanceY(g1,g-1) = 72.25
    c: DistanceX(g1,g1) = 39.5
    c: DistanceY(g4,g4) = 1
    c: DistanceY(g0,g0) = 17.5
FEATURE [PartDesign::Pad] Pad034
  Direction = (0,0,1)
  Length = 12
  Length2 = -3
  Placement = pos=(0,0,-55) rot=(0,0,1;0rad)
  Profile = -> Sketch095
  ReferenceAxis = -> Sketch095 [N_Axis]
  Refine = true
  Reversed = true
  Suppressed = false
  Type = 4
FEATURE [PartDesign::Pocket] Pocket040
  BaseFeature = -> Pad034
  Direction = (0,0,1)
  Length = 7
  Length2 = 5
  Placement = pos=(0,0,-55) rot=(0,0,1;0rad)
  Profile = -> Sketch091
  ReferenceAxis = -> Sketch091 [N_Axis]
  Refine = true
  Suppressed = false
  Type = 0
FEATURE [Sketcher::SketchObject] Sketch090  label="FanPortSk"
  ArcFitTolerance = 1e-06
  AttachmentSupport = -> [Pocket040]
  FullyConstrained = true
  MakeInternals = false
  MapMode = 5
  Placement = pos=(0,0,-58) rot=(0,0,1;0rad)
  sketch-geometry (10):
    g0: LineSegment StartX=-29.5 StartY=-72.25 StartZ=0 EndX=-29.5 EndY=-54.75 EndZ=0
    g1: LineSegment StartX=-29.5 StartY=-54.75 StartZ=0 EndX=-6.5 EndY=-54.75 EndZ=0
    g2: LineSegment StartX=-6.5 StartY=-54.75 StartZ=0 EndX=-6.5 EndY=-72.25 EndZ=0
    g3: LineSegment StartX=-6.5 StartY=-72.25 StartZ=0 EndX=-29.5 EndY=-72.25 EndZ=0
    g4: LineSegment StartX=-28.5 StartY=-71.25 StartZ=0 EndX=-7.5 EndY=-71.25 EndZ=0
    g5: LineSegment StartX=-7.5 StartY=-71.25 StartZ=0 EndX=-7.5 EndY=-55.75 EndZ=0
    g6: LineSegment StartX=-7.5 StartY=-55.75 StartZ=0 EndX=-28.5 EndY=-55.75 EndZ=0
    g7: LineSegment StartX=-28.5 StartY=-55.75 StartZ=0 EndX=-28.5 EndY=-71.25 EndZ=0
    g8: LineSegment [constr] StartX=-29.5 StartY=-72.25 StartZ=0 EndX=-28.5 EndY=-71.25 EndZ=0
    g9: LineSegment [constr] StartX=-28.5 StartY=-55.75 StartZ=0 EndX=-29.5 EndY=-54.75 EndZ=0
  constraints (26):
    c: Coincident(g0,g1)
    c: Coincident(g1,g2)
    c: Coincident(g2,g3)
    c: Coincident(g3,g0)
    c: Vertical(g2)
    c: Horizontal(g1)
    c: Horizontal(g3)
    c: Coincident(g4,g5)
    c: Coincident(g5,g6)
    c: Coincident(g6,g7)
    c: Coincident(g7,g4)
    c: Horizontal(g4)
    c: Horizontal(g6)
    c: Vertical(g5)
    c: Vertical(g7)
    c: Coincident(g0,g-4)
    c: Coincident(g0,g-4)
    c: DistanceX(g3,g3) = 23
    c: DistanceY(g7,g7) = 15.5
    c: DistanceX(g0,g6) = 1
    c: DistanceX(g5,g1) = 1
    c: Coincident(g8,g0)
    c: Coincident(g8,g4)
    c: Coincident(g9,g6)
    c: Coincident(g9,g0)
    c: Equal(g8,g9)
FEATURE [PartDesign::Pad] Pad033  label="FanPortPd"
  BaseFeature = -> Pocket040
  Direction = (0,0,1)
  Length = 2.6
  Length2 = 6
  Placement = pos=(0,0,-55) rot=(0,0,1;0rad)
  Profile = -> Sketch090
  ReferenceAxis = -> Sketch090 [N_Axis]
  Refine = true
  Suppressed = false
  Type = 0
FEATURE [PartDesign::Pocket] Pocket041
  BaseFeature = -> Pad033
  Direction = (0,0,-1)
  Length = 2
  Length2 = 5
  Placement = pos=(0,0,-55) rot=(0,0,1;0rad)
  Profile = -> Pad033 [Face20]
  Refine = true
  Suppressed = false
  Type = 0
FEATURE [Sketcher::SketchObject] Sketch092  label="OutLoft01"
  ArcFitTolerance = 1e-06
  AttachmentSupport = -> [Pocket041]
  ExternalGeometry = -> [Pocket041]
  FullyConstrained = true
  MakeInternals = false
  MapMode = 5
  Placement = pos=(0,-53.75,-55) rot=(0,0.707107,0.707107;3.14159rad)
  sketch-geometry (8):
    g0: LineSegment StartX=-10 StartY=-3 StartZ=0 EndX=-10 EndY=-12 EndZ=0
    g1: LineSegment StartX=-10 StartY=-12 StartZ=0 EndX=10 EndY=-12 EndZ=0
    g2: LineSegment StartX=10 StartY=-12 StartZ=0 EndX=10 EndY=-3 EndZ=0
    g3: LineSegment StartX=10 StartY=-3 StartZ=0 EndX=-10 EndY=-3 EndZ=0
    g4: LineSegment StartX=-9 StartY=-4 StartZ=0 EndX=-9 EndY=-11 EndZ=0
    g5: LineSegment StartX=-9 StartY=-11 StartZ=0 EndX=9 EndY=-11 EndZ=0
    g6: LineSegment StartX=9 StartY=-11 StartZ=0 EndX=9 EndY=-4 EndZ=0
    g7: LineSegment StartX=9 StartY=-4 StartZ=0 EndX=-9 EndY=-4 EndZ=0
  constraints (20):
    c: Coincident(g0,g1)
    c: Coincident(g1,g2)
    c: Coincident(g2,g3)
    c: Coincident(g3,g0)
    c: Vertical(g0)
    c: Vertical(g2)
    c: Horizontal(g1)
    c: Horizontal(g3)
    c: Coincident(g0,g-3)
    c: Coincident(g1,g-4)
    c: Coincident(g4,g5)
    c: Coincident(g5,g6)
    c: Coincident(g6,g7)
    c: Coincident(g7,g4)
    c: Vertical(g4)
    c: Vertical(g6)
    c: Horizontal(g5)
    c: Horizontal(g7)
    c: Coincident(g4,g-5)
    c: Coincident(g5,g-6)
FEATURE [Sketcher::SketchObject] Sketch093  label="0utLoft02"
  ArcFitTolerance = 1e-06
  AttachmentOffset = pos=(0,-6,11) rot=(1,0,0;0.645772rad)
  AttachmentSupport = -> [Pocket041]
  FullyConstrained = false
  MakeInternals = false
  MapMode = 5
  Placement = pos=(0,-42.75,-61) rot=(0,0.894934,0.446198;3.14159rad)
  sketch-geometry (9):
    g0: LineSegment StartX=-10 StartY=-5.44821 StartZ=0 EndX=-10 EndY=-11.4482 EndZ=0
    g1: LineSegment StartX=-10 StartY=-11.4482 StartZ=0 EndX=10 EndY=-11.4482 EndZ=0
    g2: LineSegment StartX=10 StartY=-11.4482 StartZ=0 EndX=10 EndY=-5.44821 EndZ=0
    g3: LineSegment StartX=10 StartY=-5.44821 StartZ=0 EndX=-10 EndY=-5.44821 EndZ=0
    g4: LineSegment StartX=-9 StartY=-6.44821 StartZ=0 EndX=-9 EndY=-10.4482 EndZ=0
    g5: LineSegment StartX=-9 StartY=-10.4482 StartZ=0 EndX=9 EndY=-10.4482 EndZ=0
    g6: LineSegment StartX=9 StartY=-10.4482 StartZ=0 EndX=9 EndY=-6.44821 EndZ=0
    g7: LineSegment StartX=9 StartY=-6.44821 StartZ=0 EndX=-9 EndY=-6.44821 EndZ=0
    g8: LineSegment [constr] StartX=-10 StartY=-8.44821 StartZ=0 EndX=10 EndY=-8.44821 EndZ=0
  constraints (22):
    c: Coincident(g0,g1)
    c: Coincident(g1,g2)
    c: Coincident(g2,g3)
    c: Coincident(g3,g0)
    c: Vertical(g0)
    c: Vertical(g2)
    c: Horizontal(g1)
    c: Coincident(g4,g5)
    c: Coincident(g5,g6)
    c: Coincident(g6,g7)
    c: Coincident(g7,g4)
    c: Vertical(g6)
    c: Horizontal(g5)
    c: Symmetric(g0,g2,g-2)
    c: Symmetric(g4,g6,g-2)
    c: DistanceX(g3,g3) = 20
    c: Symmetric(g0,g0,g8)
    c: Symmetric(g2,g2,g8)
    c: Symmetric(g4,g4,g8)
    c: DistanceY(g0,g4) = 1
    c: DistanceX(g5,g1) = 1
    c: DistanceY(g5,g6) = 4
FEATURE [PartDesign::AdditiveLoft] AdditiveLoft001
  BaseFeature = -> Pocket041
  Closed = false
  Placement = pos=(0,0,-55) rot=(0,0,1;0rad)
  Profile = -> Sketch092
  Refine = true
  Ruled = false
  Sections = -> [Sketch093]
  Suppressed = false
FEATURE [Sketcher::SketchObject] Sketch094
  ArcFitTolerance = 1e-06
  AttachmentSupport = -> [Pocket041]
  ExternalGeometry = -> [Binder019,Pocket041]
  FullyConstrained = true
  MakeInternals = false
  MapMode = 5
  Placement = pos=(0,0,-55.4) rot=(0,0,1;0rad)
  sketch-geometry (14):
    g0: LineSegment StartX=-23 StartY=-54.75 StartZ=0 EndX=-23 EndY=-48 EndZ=0
    g1: LineSegment StartX=23 StartY=-48 StartZ=0 EndX=23 EndY=-54.75 EndZ=0
    g2: LineSegment StartX=-23 StartY=-54.75 StartZ=0 EndX=-15 EndY=-54.75 EndZ=0
    g3: LineSegment StartX=-6.5 StartY=-54.75 StartZ=0 EndX=15 EndY=-54.75 EndZ=0
    g4: ArcOfCircle CenterX=-19 CenterY=-48 CenterZ=0 NormalX=0 NormalY=0 NormalZ=1 AngleXU=0 Radius=4 StartAngle=-9e-16 EndAngle=3.14159
    g5: ArcOfCircle CenterX=19 CenterY=-48 CenterZ=0 NormalX=0 NormalY=0 NormalZ=1 AngleXU=0 Radius=4 StartAngle=-9e-16 EndAngle=3.14159
    g6: LineSegment StartX=15 StartY=-48 StartZ=0 EndX=15 EndY=-54.75 EndZ=0
    g7: LineSegment StartX=-15 StartY=-48 StartZ=0 EndX=-15 EndY=-54.75 EndZ=0
    g8: LineSegment StartX=-6.5 StartY=-54.75 StartZ=0 EndX=-6.5 EndY=-72.25 EndZ=0
    g9: LineSegment StartX=23 StartY=-54.75 StartZ=0 EndX=23 EndY=-72.25 EndZ=0
    g10: LineSegment [constr] StartX=15 StartY=-54.75 StartZ=0 EndX=23 EndY=-54.75 EndZ=0
    g11: LineSegment StartX=-6.5 StartY=-72.25 StartZ=0 EndX=23 EndY=-72.25 EndZ=0
    g12: Circle CenterX=-19 CenterY=-48 CenterZ=0 NormalX=0 NormalY=0 NormalZ=1 AngleXU=0 Radius=1.7
    g13: Circle CenterX=19 CenterY=-48 CenterZ=0 NormalX=0 NormalY=0 NormalZ=1 AngleXU=0 Radius=1.7
  constraints (33):
    c: Vertical(g0)
    c: Vertical(g1)
    c: Horizontal(g3)
    c: Coincident(g2,g0)
    c: Coincident(g4,g-4)
    c: Coincident(g5,g-3)
    c: Diameter(g4) = 8
    c: Vertical(g6)
    c: Equal(g5,g4)
    c: Vertical(g7)
    c: Coincident(g9,g1)
    c: Vertical(g9)
    c: Tangent(g5,g6) = -1.5708
    c: Tangent(g5,g1) = 1.5708
    c: Tangent(g4,g0) = 1.5708
    c: Tangent(g4,g7) = 1.5708
    c: Coincident(g2,g7)
    c: Coincident(g3,g6)
    c: Coincident(g10,g3)
    c: Coincident(g10,g1)
    c: Horizontal(g10)
    c: Horizontal(g11)
    c: Coincident(g8,g11)
    c: Coincident(g9,g11)
    c: Coincident(g8,g3)
    c: Coincident(g8,g-6)
    c: PointOnObject(g2,g-5)
    c: PointOnObject(g0,g-5)
    c: Coincident(g12,g4)
    c: Diameter(g12) = 3.4
    c: Coincident(g13,g5)
    c: Equal(g13,g12)
    c: Coincident(g8,g-6)
FEATURE [PartDesign::Pad] Pad035
  BaseFeature = -> AdditiveLoft001
  Direction = (0,0,1)
  Length = 2.6
  Length2 = 10
  Placement = pos=(0,0,-55) rot=(0,0,1;0rad)
  Profile = -> Sketch094
  ReferenceAxis = -> Sketch094 [N_Axis]
  Refine = true
  Reversed = true
  Suppressed = false
  Type = 0
FEATURE [PartDesign::Chamfer] Chamfer012
  Angle = 45
  Base = -> Pad035 [Edge49]
  BaseFeature = -> Pad035
  ChamferType = 0
  FlipDirection = false
  Placement = pos=(0,0,-55) rot=(0,0,1;0rad)
  Refine = true
  Size = 0.98
  Size2 = 1
  SupportTransform = false
  Suppressed = false
  UseAllEdges = false
FEATURE [PartDesign::Fillet] Fillet012
  Base = -> Chamfer012 [Edge7]
  BaseFeature = -> Chamfer012
  Placement = pos=(0,0,-55) rot=(0,0,1;0rad)
  Radius = 16.5
  Refine = true
  SupportTransform = false
  Suppressed = false
  UseAllEdges = false
FEATURE [PartDesign::Fillet] Fillet013
  Base = -> Fillet012 [Edge89]
  BaseFeature = -> Fillet012
  Placement = pos=(0,0,-55) rot=(0,0,1;0rad)
  Radius = 10
  Refine = true
  SupportTransform = false
  Suppressed = false
  UseAllEdges = false
FEATURE [PartDesign::Fillet] Fillet014
  Base = -> Fillet013 [Edge49]
  BaseFeature = -> Fillet013
  Placement = pos=(0,0,-55) rot=(0,0,1;0rad)
  Radius = 11
  Refine = true
  SupportTransform = false
  Suppressed = false
  UseAllEdges = false
FEATURE [PartDesign::Fillet] Fillet015
  Base = -> Fillet014 [Edge41]
  BaseFeature = -> Fillet014
  Placement = pos=(0,0,-55) rot=(0,0,1;0rad)
  Radius = 5
  Refine = true
  SupportTransform = false
  Suppressed = false
  UseAllEdges = false
FEATURE [PartDesign::Fillet] Fillet016
  Base = -> Fillet015 [Edge102,Edge106]
  BaseFeature = -> Fillet015
  Placement = pos=(0,0,-55) rot=(0,0,1;0rad)
  Radius = 4
  Refine = true
  SupportTransform = false
  Suppressed = false
  UseAllEdges = false
FEATURE [PartDesign::Fillet] Fillet017
  Base = -> Fillet016 [Edge116,Edge112,Edge109,Edge111]
  BaseFeature = -> Fillet016
  Placement = pos=(0,0,-55) rot=(0,0,1;0rad)
  Radius = 1
  Refine = true
  SupportTransform = false
  Suppressed = false
  UseAllEdges = false
FEATURE [Sketcher::SketchObject] Sketch096  label="AirChannel"
  ArcFitTolerance = 1e-06
  AttachmentSupport = -> [Fillet017]
  ExternalGeometry = -> [Fillet017]
  FullyConstrained = true
  MakeInternals = false
  MapMode = 5
  Placement = pos=(0,0,-66) rot=(0,0,1;0rad)
  sketch-geometry (9):
    g0: LineSegment [constr] StartX=-18.5 StartY=-63.5 StartZ=0 EndX=-7.5 EndY=-63.5 EndZ=0
    g1: LineSegment [constr] StartX=-18.5 StartY=-54.75 StartZ=0 EndX=0 EndY=-54.75 EndZ=0
    g2: LineSegment StartX=-18.5 StartY=-63.9 StartZ=0 EndX=-7.5 EndY=-63.9 EndZ=0
    g3: LineSegment StartX=-18.5 StartY=-63.1 StartZ=0 EndX=-7.5 EndY=-63.1 EndZ=0
    g4: LineSegment StartX=-0.4 StartY=-54.75 StartZ=0 EndX=0.4 EndY=-54.75 EndZ=0
    g5: LineSegment StartX=-18.5 StartY=-63.1 StartZ=0 EndX=-18.5 EndY=-63.9 EndZ=0
    g6: LineSegment [constr] StartX=-7.5 StartY=-63.1 StartZ=0 EndX=-7.5 EndY=-63.9 EndZ=0
    g7: ArcOfCircle CenterX=-8.125 CenterY=-55.375 CenterZ=0 NormalX=0 NormalY=0 NormalZ=1 AngleXU=0 Radius=7.75024 StartAngle=4.79312 EndAngle=6.36392
    g8: ArcOfCircle CenterX=-8.125 CenterY=-55.375 CenterZ=0 NormalX=0 NormalY=0 NormalZ=1 AngleXU=0 Radius=8.54788 StartAngle=4.78557 EndAngle=6.35637
  constraints (24):
    c: Symmetric(g-3,g-3,g0)
    c: PointOnObject(g1,g-2)
    c: Horizontal(g0)
    c: Coincident(g1,g-3)
    c: Horizontal(g1)
    c: DistanceY(g2,g3) = 0.8
    c: Horizontal(g4)
    c: Coincident(g5,g3)
    c: Coincident(g5,g2)
    c: Vertical(g5)
    c: DistanceX(g4,g4) = 0.8
    c: Coincident(g6,g3)
    c: Distance(g6,g6) = 0.8
    c: Symmetric(g2,g3,g0)
    c: DistanceX(g0,g0) = 11
    c: Symmetric(g2,g3,g0)
    c: Vertical(g6)
    c: Coincident(g7,g3)
    c: Coincident(g2,g6)
    c: Symmetric(g4,g4,g1)
    c: Coincident(g7,g4)
    c: Coincident(g8,g7)
    c: Coincident(g8,g2)
    c: Coincident(g8,g4)
FEATURE [PartDesign::Pad] Pad036
  BaseFeature = -> Fillet017
  Direction = (0,0,1)
  Length = 10
  Length2 = 10
  Placement = pos=(0,0,-55) rot=(0,0,1;0rad)
  Profile = -> Sketch096
  ReferenceAxis = -> Sketch096 [N_Axis]
  Refine = true
  Suppressed = false
  Type = 3
  UpToFace = -> Fillet017 [Face1]
FEATURE [Sketcher::SketchObject] Sketch097
  ArcFitTolerance = 1e-06
  AttachmentSupport = -> [Pad036]
  ExternalGeometry = -> [Pad036]
  FullyConstrained = true
  MakeInternals = false
  MapMode = 5
  Placement = pos=(0,0,-55.4) rot=(0,0,1;0rad)
  sketch-geometry (4):
    g0: LineSegment StartX=-7.5 StartY=-63.1 StartZ=0 EndX=-10 EndY=-63.1 EndZ=0
    g1: LineSegment StartX=-10 StartY=-63.1 StartZ=0 EndX=-10 EndY=-63.9 EndZ=0
    g2: LineSegment StartX=-10 StartY=-63.9 StartZ=0 EndX=-7.5 EndY=-63.9 EndZ=0
    g3: LineSegment StartX=-7.5 StartY=-63.9 StartZ=0 EndX=-7.5 EndY=-63.1 EndZ=0
  constraints (11):
    c: Coincident(g0,g1)
    c: Coincident(g1,g2)
    c: Coincident(g2,g3)
    c: Coincident(g3,g0)
    c: Horizontal(g0)
    c: Horizontal(g2)
    c: Vertical(g1)
    c: Vertical(g3)
    c: Coincident(g0,g-3)
    c: PointOnObject(g1,g-4)
    c: DistanceX(g2,g2) = 2.5
FEATURE [PartDesign::Pocket] Pocket042
  BaseFeature = -> Pad036
  Direction = (0,0,-1)
  Length = 2
  Length2 = 5
  Placement = pos=(0,0,-55) rot=(0,0,1;0rad)
  Profile = -> Sketch097
  ReferenceAxis = -> Sketch097 [N_Axis]
  Refine = true
  Suppressed = false
  Type = 0
FEATURE [PartDesign::Body] Body033  label="Body"
  AllowCompound = false
  Group = -> [Binder018,Binder019,DatumPlane003,Sketch081,Sketch082,Sketch083,Sketch095,Pad034,Pocket040,Sketch090,Pad033,Sketch091,Pocket041,Sketch092,Sketch093,AdditiveLoft001,Sketch094,Pad035,Chamfer012,Fillet012,Fillet013,Fillet014,Fillet015,Fillet016,Fillet017,Sketch096,Pad036,Sketch097,Pocket042]
  Origin = -> Origin054
  Tip = -> Pocket042
FEATURE [App::Part] Part020  label="SimplePartCoolingDuct"
  Group = -> [Body033]
  Origin = -> Origin053
FEATURE [Sketcher::SketchObject] Sketch098  label="ConductorCutout"
  ArcFitTolerance = 1e-06
  AttachmentSupport = -> [Fillet010]
  ExternalGeometry = -> [Fillet010]
  FullyConstrained = true
  MakeInternals = false
  MapMode = 5
  Placement = pos=(0,0,3.6) rot=(0,0,1;0rad)
  sketch-geometry (5):
    g0: ArcOfCircle CenterX=5.7 CenterY=-24.35 CenterZ=0 NormalX=0 NormalY=0 NormalZ=1 AngleXU=0 Radius=3 StartAngle=1.5708 EndAngle=4.71239
    g1: LineSegment StartX=5.7 StartY=-21.35 StartZ=0 EndX=12.75 EndY=-21.35 EndZ=0
    g2: LineSegment StartX=5.7 StartY=-27.35 StartZ=0 EndX=12.75 EndY=-27.35 EndZ=0
    g3: LineSegment [constr] StartX=5.7 StartY=-21.35 StartZ=0 EndX=5.7 EndY=-27.35 EndZ=0
    g4: LineSegment StartX=12.75 StartY=-21.35 StartZ=0 EndX=12.75 EndY=-27.35 EndZ=0
  constraints (13):
    c: Coincident(g0,g-4)
    c: PointOnObject(g1,g-3)
    c: Horizontal(g1)
    c: Horizontal(g2)
    c: Tangent(g0,g2) = -1.5708
    c: Coincident(g0,g1)
    c: Coincident(g3,g0)
    c: Coincident(g3,g0)
    c: Vertical(g3)
    c: DistanceY(g2,g1) = 6
    c: PointOnObject(g2,g-3)
    c: Coincident(g4,g1)
    c: Coincident(g4,g2)
FEATURE [PartDesign::Pocket] Pocket043  label="ConductorPk"
  BaseFeature = -> Fillet010
  Direction = (0,0,-1)
  Length = 1
  Length2 = 5
  Profile = -> Sketch098
  ReferenceAxis = -> Sketch098 [N_Axis]
  Refine = true
  Suppressed = false
  Type = 0
FEATURE [PartDesign::Body] Body015
  AllowCompound = false
  Group = -> [Binder,Binder015,Sketch031,Pad008,Sketch032,Sketch033,Sketch034,Sketch035,Pocket014,Fillet007,Pocket019,Pocket020,Hole004,Fillet010,Sketch098,Pocket043]
  Origin = -> Origin030
  Tip = -> Pocket043
FEATURE [App::Part] Part014  label="HotendMountPlate"
  Group = -> [Body015]
  Origin = -> Origin029
  Placement = pos=(0,0,-18) rot=(0,0,1;0rad)
FEATURE [Spreadsheet::Sheet] Spreadsheet  label="Properties"
  cells = A2='M3 Heat Set Inset Dia; B2(M3Inset)==5.5 mm; A3='M3 Heat Set Inset Depth; B3(M3InsetDepth)==4 mm; A4='M3 Counter Sink Dia; B4(M3CsinkDia)=6.1
FEATURE [PartDesign::SubShapeBinder] Binder020  label="HeatBreakFanBinder001"
  BindCopyOnChange = 0
  BindMode = 0
  ClaimChildren = false
  Context = -> Part018 [Body026.Binder020.]
  Fuse = false
  MakeFace = true
  OffsetFill = false
  OffsetIntersection = false
  OffsetJoinType = 0
  OffsetOpenResult = false
  PartialLoad = false
  Placement = pos=(-24,0,0) rot=(0,0,1;0rad)
  Refine = true
  Relative = true
  Support = -> [Sketch076[Edge2,Edge1,Edge3,Edge4]]
  _Version = 2
FEATURE [PartDesign::Hole] Hole006  label="HeatBreakFanInsets001"
  BaseFeature = -> Pocket033
  CustomThreadClearance = 0
  Depth = 5
  DepthType = 0
  Diameter = 3.4
  DrillForDepth = false
  DrillPoint = 0
  DrillPointAngle = 118
  HoleCutCountersinkAngle = 90
  HoleCutCustomValues = false
  HoleCutDepth = 4
  HoleCutDiameter = 5.5
  HoleCutType = 1
  ModelThread = false
  Profile = -> Binder020 [Face3,Face4,Face2]
  Refine = true
  Reversed = true
  Suppressed = false
  Tapered = false
  TaperedAngle = 90
  ThreadClass = 0
  ThreadDepth = 5
  ThreadDepthType = 0
  ThreadDirection = 0
  ThreadFit = 0
  ThreadSize = 9
  ThreadType = 1
  Threaded = false
  UseCustomThreadClearance = false
  expr: HoleCutDepth = <<Properties>>.M3InsetDepth
  expr: HoleCutDiameter = <<Properties>>.M3Inset
FEATURE [PartDesign::Pocket] Pocket035  label="MountPlateInsets"
  BaseFeature = -> Hole006
  Direction = (0,0,-1)
  Length = 3.8
  Length2 = 5
  Profile = -> Binder012
  Refine = true
  Suppressed = false
  Type = 0
FEATURE [PartDesign::Hole] Hole005  label="BasePlateInsets"
  BaseFeature = -> Pocket035
  CustomThreadClearance = 0
  Depth = 25
  DepthType = 0
  Diameter = 3.4
  DrillForDepth = false
  DrillPoint = 1
  DrillPointAngle = 118
  HoleCutCountersinkAngle = 90
  HoleCutCustomValues = false
  HoleCutDepth = 15.5
  HoleCutDiameter = 6.1
  HoleCutType = 1
  ModelThread = false
  Profile = -> Binder011
  Refine = true
  Reversed = true
  Suppressed = false
  Tapered = false
  TaperedAngle = 90
  ThreadClass = 0
  ThreadDepth = 25
  ThreadDepthType = 0
  ThreadDirection = 0
  ThreadFit = 0
  ThreadSize = 9
  ThreadType = 1
  Threaded = false
  UseCustomThreadClearance = false
FEATURE [PartDesign::Chamfer] Chamfer004  label="TopPlateSpaceChamfer"
  Angle = 45
  Base = -> Hole005 [Edge79,Edge106]
  BaseFeature = -> Hole005
  ChamferType = 0
  FlipDirection = false
  Refine = true
  Size = 4
  Size2 = 1
  SupportTransform = false
  Suppressed = false
  UseAllEdges = false
FEATURE [PartDesign::Chamfer] Chamfer005  label="FrontBridgeChamfer"
  Angle = 45
  Base = -> Chamfer004 [Edge101,Edge91,Edge199]
  BaseFeature = -> Chamfer004
  ChamferType = 0
  FlipDirection = false
  Refine = true
  Size = 2.99
  Size2 = 1
  SupportTransform = false
  Suppressed = false
  UseAllEdges = false
FEATURE [PartDesign::Chamfer] Chamfer006  label="EdgesChamfer"
  Angle = 45
  Base = -> Chamfer005 [Edge154,Edge112,Edge88,Edge240,Edge242,Edge289,Edge271,Edge62,Edge148,Edge5]
  BaseFeature = -> Chamfer005
  ChamferType = 0
  FlipDirection = false
  Refine = true
  Size = 2
  Size2 = 1
  SupportTransform = false
  Suppressed = false
  UseAllEdges = false
FEATURE [PartDesign::Pocket] Pocket037  label="CoolingCableGuide"
  BaseFeature = -> Chamfer006
  Direction = (-1,-1e-16,1e-16)
  Length = 4
  Length2 = 5
  Profile = -> Sketch075
  ReferenceAxis = -> Sketch075 [N_Axis]
  Refine = true
  Suppressed = false
  Type = 0
FEATURE [PartDesign::Chamfer] Chamfer008  label="CoolingCableGuideCh"
  Angle = 45
  Base = -> Pocket037 [Edge126]
  BaseFeature = -> Pocket037
  ChamferType = 0
  FlipDirection = false
  Refine = true
  Size = 2
  Size2 = 1
  SupportTransform = false
  Suppressed = false
  UseAllEdges = false
FEATURE [PartDesign::Chamfer] Chamfer009  label="FatBaseCh"
  Angle = 45
  Base = -> Chamfer008 [Edge53]
  BaseFeature = -> Chamfer008
  ChamferType = 0
  FlipDirection = false
  Refine = true
  Size = 3
  Size2 = 1
  SupportTransform = false
  Suppressed = false
  UseAllEdges = false
FEATURE [PartDesign::Pad] Pad031
  BaseFeature = -> Chamfer009
  Direction = (6.99e-14,-1,0)
  Length = 3
  Length2 = 10
  Profile = -> Chamfer009 [Face7]
  Refine = true
  Suppressed = false
  Type = 0
FEATURE [PartDesign::Chamfer] Chamfer010  label="SharpEdgesCh"
  Angle = 45
  Base = -> Pad031 [Edge138,Edge75,Edge78,Edge182,Edge176,Edge179,Edge335,Edge190,Edge210,Edge21,Edge15]
  BaseFeature = -> Pad031
  ChamferType = 0
  FlipDirection = false
  Refine = true
  Size = 0.5
  Size2 = 1
  SupportTransform = false
  Suppressed = false
  UseAllEdges = false
FEATURE [PartDesign::Chamfer] Chamfer  label="PartCoolingInletCh"
  Angle = 45
  Base = -> Chamfer010 [Edge5,Edge7]
  BaseFeature = -> Chamfer010
  ChamferType = 0
  FlipDirection = false
  Refine = true
  Size = 0.8
  Size2 = 1
  SupportTransform = false
  Suppressed = false
  UseAllEdges = false
FEATURE [PartDesign::Body] Body026  label="BooleanBody"
  AllowCompound = false
  Group = -> [Binder011,Binder010,Binder012,Binder013,Boolean,Sketch073,Sketch070,Pocket029,Pad028,Pocket030,Pad029,Pocket031,Pocket032,Pocket033,Binder020,Hole006,Pocket035,Hole005,Chamfer004,Chamfer005,Chamfer006,Sketch075,Pocket037,Chamfer008,Chamfer009,Pad031,Chamfer010,Sketch074,Chamfer]
  Origin = -> Origin045
  Tip = -> Chamfer
FEATURE [App::Part] Part018  label="CombinedTool"
  Group = -> [Body026]
  Origin = -> Origin044
FEATURE [App::DocumentObjectGroup] Group002  label="Base Sketches"
  Group = -> [Sketch,Sketch006,Sketch076,Sketch042,Sketch043,Sketch045,Sketch046]
